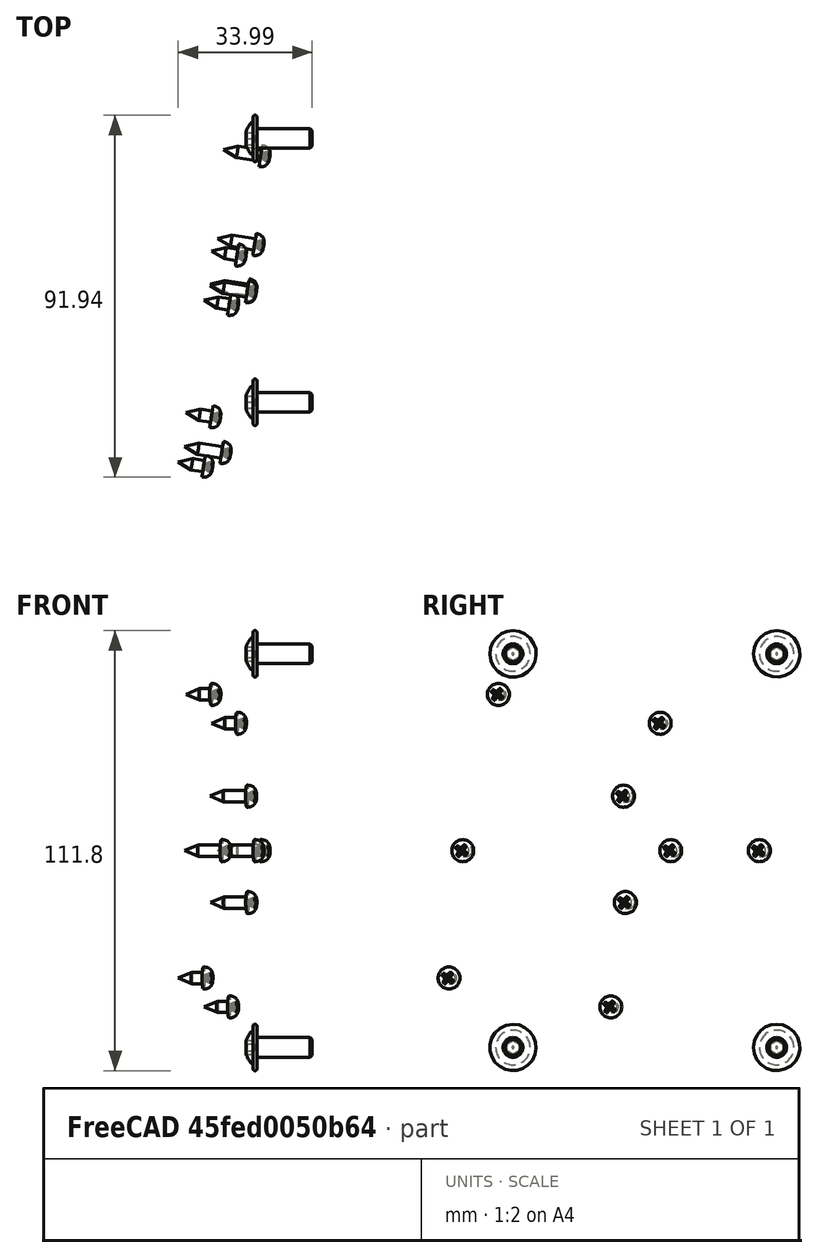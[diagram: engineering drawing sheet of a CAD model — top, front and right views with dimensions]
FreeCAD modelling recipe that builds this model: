
FCSTD DOCUMENT  (FreeCAD 1.0R39319 (Git))
Label: Assy_Stack_Module_Cover_forInserts
License: All rights reserved
LicenseURL: https://en.wikipedia.org/wiki/All_rights_reserved
objects: Part::FeaturePython×13, TechDraw::DrawViewBalloon×13, App::Link×8, TechDraw::DrawProjGroupItem×7, App::DocumentObjectGroup×3, TechDraw::DrawViewDimension×3, TechDraw::DrawSVGTemplate×2, TechDraw::DrawPage×2, PartDesign::CoordinateSystem×1, App::FeaturePython×1, App::Part×1, Spreadsheet::Sheet×1, TechDraw::DrawViewSpreadsheet×1, TechDraw::DrawProjGroup×1
note: 20 computed .brp shape members not serialized (recipe doc carries the construction recipe); baked Part::Feature solids carry a one-line shape summary decoded from their .brp
EXTERNAL_REF file=../../Part/Print/Stack_Module_Cover_forInserts.FCStd obj=stack_att
EXTERNAL_REF file=../../Part/Print/Stack_Module_Cover_forInserts.FCStd obj=Part
EXTERNAL_REF file=../../Part/Purchase/M5x12_Sleeve_Nut.FCStd obj=LCS_1
EXTERNAL_REF file=../../Part/Print/Stack_Module_Cover_forInserts.FCStd obj=sleevenut_att1
EXTERNAL_REF file=../../Part/Purchase/M5x12_Sleeve_Nut.FCStd obj=Part
EXTERNAL_REF file=../../Part/Print/Stack_Module_Cover_forInserts.FCStd obj=sleevenut_att2
EXTERNAL_REF file=../../Part/Print/Stack_Module_Cover_forInserts.FCStd obj=sleevenut_att3
EXTERNAL_REF file=../../Part/Print/Stack_Module_Cover_forInserts.FCStd obj=sleevenut_att4
EXTERNAL_REF file=../../Part/Print/Stack_Module_Cover_LogoTee.FCStd obj=LCS_1
EXTERNAL_REF file=../../Part/Print/Stack_Module_Cover_forInserts.FCStd obj=tee_att
EXTERNAL_REF file=../../Part/Print/Stack_Module_Cover_LogoTee.FCStd obj=Part
EXTERNAL_REF file=../../Part/Print/Stack_Module_Cover_LogoBall.FCStd obj=LCS_1
EXTERNAL_REF file=../../Part/Print/Stack_Module_Cover_forInserts.FCStd obj=Logo_att
EXTERNAL_REF file=../../Part/Print/Stack_Module_Cover_LogoBall.FCStd obj=Part
EXTERNAL_REF file=../../Part/Print/Stack_Module_Cover_insert.FCStd obj=LCS_1
EXTERNAL_REF file=../../Part/Print/Stack_Module_Cover_insert.FCStd obj=Part

FEATURE [App::DocumentObjectGroup] Parts
FEATURE [PartDesign::CoordinateSystem] LCS_Origin
  AttacherType = Attacher::AttachEngine3D
  AttachmentSupport = -> [X_Axis]
  MapMode = 2
FEATURE [App::DocumentObjectGroup] Constraints
FEATURE [App::FeaturePython] Variables  # WARN: FeaturePython — macro-defined, semantics opaque (R4)
  Type = App::PropertyContainer
FEATURE [App::DocumentObjectGroup] Configurations
FEATURE [App::Link] Stack_Module_Cover_twoInserts
  AttachedBy = #stack_att
  AttachedTo = Parent Assembly#LCS_Origin
  AttachmentOffset = pos=(0,0,0) rot=(0.57735,0.57735,-0.57735;4.18879rad)
  LinkPlacement = pos=(-4e-16,62.5,-63.5) rot=(0.57735,0.57735,-0.57735;2.0944rad)
  LinkedObject = -> <external ../../Part/Print/Stack_Module_Cover_forInserts.FCStd>#Part
  Placement = pos=(-4e-16,62.5,-63.5) rot=(0.57735,0.57735,-0.57735;2.0944rad)
  SolverId = Asm4EE
  expr: Placement = LCS_Origin.Placement * AttachmentOffset * Stack_Module_Cover_forInserts#stack_att.Placement ^ -1
FEATURE [App::Link] M5x12_Sleeve_Nut
  AttachedBy = #LCS_1
  AttachedTo = Stack_Module_Cover_twoInserts#sleevenut_att1
  AttachmentOffset = pos=(0,0,0) rot=(0,1,0;3.14159rad)
  LinkPlacement = pos=(-8,116,-130) rot=(-0.707107,0,0.707107;3.14159rad)
  LinkedObject = -> <external ../../Part/Purchase/M5x12_Sleeve_Nut.FCStd>#Part
  Placement = pos=(-8,116,-130) rot=(-0.707107,0,0.707107;3.14159rad)
  SolverId = Asm4EE
  expr: Placement = Stack_Module_Cover_twoInserts.Placement * Stack_Module_Cover_forInserts#sleevenut_att1.Placement * AttachmentOffset * M5x12_Sleeve_Nut#LCS_1.Placement ^ -1
FEATURE [App::Link] M5x12_Sleeve_Nut001
  AttachedBy = #LCS_1
  AttachedTo = Stack_Module_Cover_twoInserts#sleevenut_att2
  AttachmentOffset = pos=(0,0,0) rot=(0,1,0;3.14159rad)
  LinkPlacement = pos=(-8,2.84e-14,-127) rot=(-0.707107,0,0.707107;3.14159rad)
  LinkedObject = -> <external ../../Part/Purchase/M5x12_Sleeve_Nut.FCStd>#Part
  Placement = pos=(-8,2.84e-14,-127) rot=(-0.707107,0,0.707107;3.14159rad)
  SolverId = Asm4EE
  expr: Placement = Stack_Module_Cover_twoInserts.Placement * Stack_Module_Cover_forInserts#sleevenut_att2.Placement * AttachmentOffset * M5x12_Sleeve_Nut#LCS_1.Placement ^ -1
FEATURE [App::Link] M5x12_Sleeve_Nut002
  AttachedBy = #LCS_1
  AttachedTo = Stack_Module_Cover_twoInserts#sleevenut_att3
  LinkPlacement = pos=(-8,1.42e-14,-1.47e-14) rot=(0,-1,0;1.5708rad)
  LinkedObject = -> <external ../../Part/Purchase/M5x12_Sleeve_Nut.FCStd>#Part
  Placement = pos=(-8,1.42e-14,-1.47e-14) rot=(0,-1,0;1.5708rad)
  SolverId = Asm4EE
  expr: Placement = Stack_Module_Cover_twoInserts.Placement * Stack_Module_Cover_forInserts#sleevenut_att3.Placement * AttachmentOffset * M5x12_Sleeve_Nut#LCS_1.Placement ^ -1
FEATURE [App::Link] M5x12_Sleeve_Nut003
  AttachedBy = #LCS_1
  AttachedTo = Stack_Module_Cover_twoInserts#sleevenut_att4
  LinkPlacement = pos=(-8,116,3) rot=(0,-1,0;1.5708rad)
  LinkedObject = -> <external ../../Part/Purchase/M5x12_Sleeve_Nut.FCStd>#Part
  Placement = pos=(-8,116,3) rot=(0,-1,0;1.5708rad)
  SolverId = Asm4EE
  expr: Placement = Stack_Module_Cover_twoInserts.Placement * Stack_Module_Cover_forInserts#sleevenut_att4.Placement * AttachmentOffset * M5x12_Sleeve_Nut#LCS_1.Placement ^ -1
FEATURE [App::Link] Stack_Module_Cover_LogoTee
  AttachedBy = #LCS_1
  AttachedTo = Stack_Module_Cover_twoInserts#tee_att
  LinkPlacement = pos=(-22.5417,59.55,-63.5) rot=(-0.706014,0.055565,0.706014;3.03058rad)
  LinkedObject = -> <external ../../Part/Print/Stack_Module_Cover_LogoTee.FCStd>#Part
  Placement = pos=(-22.5417,59.55,-63.5) rot=(-0.706014,0.055565,0.706014;3.03058rad)
  SolverId = Asm4EE
  expr: Placement = Stack_Module_Cover_twoInserts.Placement * Stack_Module_Cover_forInserts#tee_att.Placement * AttachmentOffset * Stack_Module_Cover_LogoTee#LCS_1.Placement ^ -1
FEATURE [App::Link] Stack_Module_Cover_LogoBall
  AttachedBy = #LCS_1
  AttachedTo = Stack_Module_Cover_twoInserts#Logo_att
  AttachmentOffset = pos=(0,0,0) rot=(0,1,0;3.14159rad)
  LinkPlacement = pos=(-22.7075,58.503,-63.5) rot=(-0.706014,0.055565,0.706014;3.03058rad)
  LinkedObject = -> <external ../../Part/Print/Stack_Module_Cover_LogoBall.FCStd>#Part
  Placement = pos=(-22.7075,58.503,-63.5) rot=(-0.706014,0.055565,0.706014;3.03058rad)
  SolverId = Asm4EE
  expr: Placement = Stack_Module_Cover_twoInserts.Placement * Stack_Module_Cover_forInserts#Logo_att.Placement * AttachmentOffset * Stack_Module_Cover_LogoBall#LCS_1.Placement ^ -1
FEATURE [App::Link] Stack_Module_Cover_insert
  AttachedBy = #LCS_1
  AttachedTo = Stack_Module_Cover_twoInserts#Logo_att
  LinkPlacement = pos=(-22.7075,58.503,-63.5) rot=(0.553126,-0.543555,0.631347;3.98786rad)
  LinkedObject = -> <external ../../Part/Print/Stack_Module_Cover_insert.FCStd>#Part
  Placement = pos=(-22.7075,58.503,-63.5) rot=(0.553126,-0.543555,0.631347;3.98786rad)
  SolverId = Asm4EE
  expr: Placement = Stack_Module_Cover_twoInserts.Placement * Stack_Module_Cover_forInserts#Logo_att.Placement * AttachmentOffset * Stack_Module_Cover_insert#LCS_1.Placement ^ -1
FEATURE [Part::FeaturePython] Screw  label="M5x14-Screw"  # WARN: FeaturePython — macro-defined, semantics opaque (R4)
  BaseObject = -> Stack_Module_Cover_twoInserts [Body.Pocket022.Edge443]
  Diameter = 3
  Invert = false
  LeftHanded = false
  Length = 3
  LengthCustom = 14
  MatchOuter = false
  OffsetAngle = 0
  Placement = pos=(-4.5,113.5,-13.5) rot=(0,-1,0;1.5708rad)
  Thread = false
  Type = 86
FEATURE [Part::FeaturePython] Screw001  label="M5x14-Screw007"  # WARN: FeaturePython — macro-defined, semantics opaque (R4)
  BaseObject = -> Stack_Module_Cover_twoInserts [Body.Pocket022.Edge441]
  Diameter = 3
  Invert = false
  LeftHanded = false
  Length = 3
  LengthCustom = 14
  MatchOuter = false
  OffsetAngle = 0
  Placement = pos=(-4.5,46.5,-13.5) rot=(0,-1,0;1.5708rad)
  Thread = false
  Type = 86
FEATURE [Part::FeaturePython] Screw002  label="M5x14-Screw008"  # WARN: FeaturePython — macro-defined, semantics opaque (R4)
  BaseObject = -> Stack_Module_Cover_twoInserts [Body.Pocket022.Edge440]
  Diameter = 3
  Invert = true
  LeftHanded = false
  Length = 3
  LengthCustom = 14
  MatchOuter = false
  OffsetAngle = 0
  Placement = pos=(-4.5,46.5,-113.5) rot=(0,-1,0;1.5708rad)
  Thread = false
  Type = 86
FEATURE [Part::FeaturePython] Screw003  label="M5x14-Screw009"  # WARN: FeaturePython — macro-defined, semantics opaque (R4)
  BaseObject = -> Stack_Module_Cover_twoInserts [Body.Pocket022.Edge442]
  Diameter = 3
  Invert = true
  LeftHanded = false
  Length = 3
  LengthCustom = 14
  MatchOuter = false
  OffsetAngle = 0
  Placement = pos=(-4.5,113.5,-113.5) rot=(0,-1,0;1.5708rad)
  Thread = false
  Type = 86
FEATURE [Part::FeaturePython] Screw004  label="ST2.9x9.5-Screw"  # WARN: FeaturePython — macro-defined, semantics opaque (R4)
  BaseObject = -> Stack_Module_Cover_twoInserts [Body.Pocket022.Edge623]
  Diameter = 2
  Invert = true
  LeftHanded = false
  Length = 1
  LengthCustom = 9.5
  MatchOuter = false
  OffsetAngle = 0
  Placement = pos=(-3.55191,109.13,-63.5) rot=(0.156434,0.987688,0;1.5708rad)
  Thread = false
  Type = 81
FEATURE [Part::FeaturePython] Screw005  label="ST2.9x9.5-Screw009"  # WARN: FeaturePython — macro-defined, semantics opaque (R4)
  BaseObject = -> Stack_Module_Cover_insert [Body.Pocket001.Edge17]
  Diameter = 2
  Invert = true
  LeftHanded = false
  Length = 1
  LengthCustom = 9.5
  MatchOuter = false
  OffsetAngle = 0
  Placement = pos=(-5.0963,86.5939,-63.5) rot=(0.156434,0.987688,0;1.5708rad)
  Thread = false
  Type = 81
FEATURE [Part::FeaturePython] Screw006  label="ST2.9x9.5-Screw010"  # WARN: FeaturePython — macro-defined, semantics opaque (R4)
  BaseObject = -> Stack_Module_Cover_insert [Body.Pocket001.Edge16]
  Diameter = 2
  Invert = true
  LeftHanded = false
  Length = 1
  LengthCustom = 9.5
  MatchOuter = false
  OffsetAngle = 0
  Placement = pos=(-6.92025,75.0779,-76.6923) rot=(0.156434,0.987688,0;1.5708rad)
  Thread = false
  Type = 81
FEATURE [Part::FeaturePython] Screw007  label="ST2.9x9.5-Screw011"  # WARN: FeaturePython — macro-defined, semantics opaque (R4)
  BaseObject = -> Stack_Module_Cover_insert [Body.Pocket001.Edge18]
  Diameter = 2
  Invert = true
  LeftHanded = false
  Length = 1
  LengthCustom = 9.5
  MatchOuter = false
  OffsetAngle = 0
  Placement = pos=(-6.99407,74.6118,-49.6583) rot=(0.156434,0.987688,0;1.5708rad)
  Thread = false
  Type = 81
FEATURE [Part::FeaturePython] Screw008  label="ST2.9x9.5-Screw012"  # WARN: FeaturePython — macro-defined, semantics opaque (R4)
  BaseObject = -> Stack_Module_Cover_insert [Body.Pocket001.Edge9]
  Diameter = 2
  Invert = true
  LeftHanded = false
  Length = 1
  LengthCustom = 9.5
  MatchOuter = false
  OffsetAngle = 0
  Placement = pos=(-13.4655,33.7525,-63.5) rot=(0.156434,0.987688,0;1.5708rad)
  Thread = false
  Type = 81
FEATURE [Part::FeaturePython] Screw009  label="ST2.9x6.5-Screw"  # WARN: FeaturePython — macro-defined, semantics opaque (R4)
  BaseObject = -> Stack_Module_Cover_twoInserts [Body.Pocket022.Edge118]
  Diameter = 2
  Invert = false
  LeftHanded = false
  Length = 0
  LengthCustom = 6.5
  MatchOuter = false
  Offset = 2
  OffsetAngle = 0
  Placement = pos=(-11.5578,71.3676,-103.202) rot=(0.156434,0.987688,0;1.5708rad)
  Thread = false
  Type = 81
FEATURE [Part::FeaturePython] Screw010  label="ST2.9x6.5-Screw012"  # WARN: FeaturePython — macro-defined, semantics opaque (R4)
  BaseObject = -> Stack_Module_Cover_twoInserts [Body.Pocket022.Edge121]
  Diameter = 2
  Invert = false
  LeftHanded = false
  Length = 0
  LengthCustom = 6.5
  MatchOuter = false
  Offset = 2
  OffsetAngle = 0
  Placement = pos=(-18.0667,30.2717,-95.8654) rot=(0.156434,0.987688,0;1.5708rad)
  Thread = false
  Type = 81
FEATURE [Part::FeaturePython] Screw011  label="ST2.9x6.5-Screw013"  # WARN: FeaturePython — macro-defined, semantics opaque (R4)
  BaseObject = -> Stack_Module_Cover_twoInserts [Body.Pocket022.Edge169]
  Diameter = 2
  Invert = false
  LeftHanded = false
  Length = 0
  LengthCustom = 6.5
  MatchOuter = false
  Offset = 2
  OffsetAngle = 0
  Placement = pos=(-16.0788,42.8227,-23.798) rot=(0.156434,0.987688,0;1.5708rad)
  Thread = false
  Type = 81
FEATURE [Part::FeaturePython] Screw012  label="ST2.9x6.5-Screw014"  # WARN: FeaturePython — macro-defined, semantics opaque (R4)
  BaseObject = -> Stack_Module_Cover_twoInserts [Body.Pocket022.Edge168]
  Diameter = 2
  Invert = false
  LeftHanded = false
  Length = 0
  LengthCustom = 6.5
  MatchOuter = false
  Offset = 2
  OffsetAngle = 0
  Placement = pos=(-9.5699,83.9185,-31.1346) rot=(0.156434,0.987688,0;1.5708rad)
  Thread = false
  Type = 81
FEATURE [App::Part] Assembly  label="Assy_Stack_Module_Cover_forInserts"
  AssemblyType = Part::Link
  Group = -> [LCS_Origin,Constraints,Variables,Configurations,Stack_Module_Cover_twoInserts,M5x12_Sleeve_Nut,M5x12_Sleeve_Nut001,M5x12_Sleeve_Nut002,M5x12_Sleeve_Nut003,Stack_Module_Cover_LogoTee,Stack_Module_Cover_LogoBall,Stack_Module_Cover_insert,Screw,Screw001,Screw002,Screw003,Screw004,Screw005,Screw006,Screw007,Screw008,Screw009,Screw010,Screw011,Screw012]
  Origin = -> Origin
  Type = Assembly
FEATURE [Spreadsheet::Sheet] Spreadsheet  label="BOM"
  cells = A1=6; B1=5; C1='M3x10 mm self-tapping screw; D1==10 mm; A2=5; B2=4; C2='M3x5 mm self-tapping screw; D2==5 mm; A3=4; B3=1; C3='Stack_Module_Cover_LogoBall; D3='-; E3='PETG or PLA; A4=3; B4=1; C4='Stack_Module_Cover_LogoTee; D4='-; E4='PETG or PLA; A5=2; B5=1; C5='Stack_Module_Cover_insert; D5='-; E5='PETG or PLA, white; A6=1; B6=1; C6='Stack_Module_Cover_forInserts; D6='-; E6='PETG or PLA; A7='Position; B7='Quantity; C7='Part; D7='Dimensions; E7='Material
FEATURE [TechDraw::DrawSVGTemplate] Template
  EditableTexts = approval_person=GitHubPR; creator=Stefan; date_of_issue=20.03.2026; document_type=Assembly Drawing; general_tolerances=na; identification_number=na; language_code=EN; part_material=na; revision_index=AAA; scale=1 : 1; sheet_number=1 / 1; title=Assy_Stack_Module_Cover_forInserts
  Height = 420
  Orientation = 1
  Template = <userpath>/Documents/PiTrac/3D Printed Parts/Enclosure Version 3/Assets/PiTrac_A2_Landscape_ISO5457_minimal.svg
  Width = 594
FEATURE [TechDraw::DrawViewSpreadsheet] Sheet
  CellEnd = E7
  CellStart = A1
  Font = osifont
  LineWidth = 0.35
  LockPosition = false
  Rotation = 0
  ScaleType = 2
  Source = -> Spreadsheet
  Symbol = <blob: 7887 chars omitted>
  TextSize = 12
  X = 496.686
  Y = 106.021
FEATURE [TechDraw::DrawProjGroupItem] View
  CoarseView = false
  Direction = (-0.57735,0.57735,-0.57735)
  Focus = 100
  HardHidden = false
  IsoCount = 0
  IsoHidden = false
  IsoVisible = false
  LockPosition = false
  Perspective = false
  Rotation = 0
  RotationVector = (1,0,0)
  Scale = 0.5
  ScaleType = 2
  ScrubCount = 1
  SeamHidden = false
  SeamVisible = false
  SmoothHidden = false
  SmoothVisible = true
  Source = -> [Assembly]
  Type = 0
  X = 339.537
  XDirection = (0,-0.707106,-0.707106)
  Y = 97.1596
FEATURE [TechDraw::DrawProjGroupItem] View001  label="Front"
  CoarseView = false
  Direction = (0,1,0)
  Focus = 100
  HardHidden = false
  IsoCount = 0
  IsoHidden = false
  IsoVisible = false
  LockPosition = true
  Perspective = false
  Rotation = 0
  RotationVector = (1,0,0)
  ScaleType = 2
  ScrubCount = 1
  SeamHidden = false
  SeamVisible = false
  SmoothHidden = false
  SmoothVisible = true
  Source = -> [Assembly]
  Type = 0
  X = 0
  XDirection = (0,0,-1)
  Y = 0
FEATURE [TechDraw::DrawProjGroupItem] ProjItem  label="Left"
  CoarseView = false
  Direction = (0,1e-16,1)
  Focus = 100
  HardHidden = false
  IsoCount = 0
  IsoHidden = false
  IsoVisible = false
  LockPosition = false
  Perspective = false
  Rotation = 0
  RotationVector = (1,0,0)
  ScaleType = 0
  ScrubCount = 1
  SeamHidden = false
  SeamVisible = false
  SmoothHidden = false
  SmoothVisible = true
  Source = -> [Assembly]
  Type = 1
  X = 159
  XDirection = (0,1,-1e-16)
  Y = 0
FEATURE [TechDraw::DrawProjGroupItem] ProjItem001  label="Top"
  CoarseView = false
  Direction = (-1,0,0)
  Focus = 100
  HardHidden = false
  IsoCount = 0
  IsoHidden = false
  IsoVisible = false
  LockPosition = false
  Perspective = false
  Rotation = 0
  RotationVector = (1,0,0)
  ScaleType = 0
  ScrubCount = 1
  SeamHidden = false
  SeamVisible = false
  SmoothHidden = false
  SmoothVisible = true
  Source = -> [Assembly]
  Type = 4
  X = 0
  XDirection = (0,0,-1)
  Y = -105.76
FEATURE [TechDraw::DrawProjGroupItem] ProjItem002  label="Rear"
  CoarseView = false
  Direction = (0,-1,0)
  Focus = 100
  HardHidden = false
  IsoCount = 0
  IsoHidden = false
  IsoVisible = false
  LockPosition = false
  Perspective = false
  Rotation = 0
  RotationVector = (1,0,0)
  ScaleType = 0
  ScrubCount = 1
  SeamHidden = false
  SeamVisible = false
  SmoothHidden = false
  SmoothVisible = true
  Source = -> [Assembly]
  Type = 3
  X = 318
  XDirection = (0,0,1)
  Y = 0
FEATURE [TechDraw::DrawProjGroupItem] ProjItem003  label="Bottom"
  CoarseView = false
  Direction = (1,0,0)
  Focus = 100
  HardHidden = false
  IsoCount = 0
  IsoHidden = false
  IsoVisible = false
  LockPosition = false
  Perspective = false
  Rotation = 0
  RotationVector = (1,0,0)
  ScaleType = 0
  ScrubCount = 1
  SeamHidden = false
  SeamVisible = false
  SmoothHidden = false
  SmoothVisible = true
  Source = -> [Assembly]
  Type = 5
  X = 0
  XDirection = (0,0,-1)
  Y = 105.76
FEATURE [TechDraw::DrawProjGroup] ProjGroup
  Anchor = -> View001
  AutoDistribute = true
  LockPosition = false
  ProjectionType = 0
  Rotation = 0
  ScaleType = 0
  Source = -> [Assembly]
  Views = -> [View001,ProjItem,ProjItem001,ProjItem002,ProjItem003]
  X = 165.254
  Y = 222.997
  spacingX = 15
  spacingY = 15
FEATURE [TechDraw::DrawViewBalloon] Balloon
  BubbleShape = 0
  EndType = 0
  EndTypeScale = 1
  KinkLength = 5
  LockPosition = false
  OriginX = -41.8317
  OriginY = -30.0185
  Rotation = 0
  ScaleType = 0
  ShapeScale = 1
  SourceView = -> ProjItem001
  Text = 1
  TextWrapLen = -1
  X = -90
  Y = -22.3266
FEATURE [TechDraw::DrawViewBalloon] Balloon001
  BubbleShape = 0
  EndType = 0
  EndTypeScale = 1
  KinkLength = 5
  LockPosition = false
  OriginX = -24.0534
  OriginY = 6.56381
  Rotation = 0
  ScaleType = 0
  ShapeScale = 1
  SourceView = -> ProjItem001
  Text = 2
  TextWrapLen = -1
  X = -90
  Y = -3.86449
FEATURE [TechDraw::DrawViewBalloon] Balloon002
  BubbleShape = 0
  EndType = 0
  EndTypeScale = 1
  KinkLength = 5
  LockPosition = false
  OriginX = -3.88181
  OriginY = -45.4036
  Rotation = 0
  ScaleType = 0
  ShapeScale = 1
  SourceView = -> Balloon001
  Text = 3
  TextWrapLen = -1
  X = -90
  Y = -46.6009
FEATURE [TechDraw::DrawViewBalloon] Balloon003
  BubbleShape = 0
  EndType = 0
  EndTypeScale = 1
  KinkLength = 5
  LockPosition = false
  OriginX = -29.8655
  OriginY = 27.4192
  Rotation = 0
  ScaleType = 0
  ShapeScale = 1
  SourceView = -> Balloon002
  Text = 4
  TextWrapLen = -1
  X = -90
  Y = 18.0165
FEATURE [TechDraw::DrawViewBalloon] Balloon004
  BubbleShape = 0
  EndType = 0
  EndTypeScale = 1
  KinkLength = 5
  LockPosition = false
  OriginX = -39.2761
  OriginY = -19.3115
  Rotation = 0
  ScaleType = 0
  ShapeScale = 1
  SourceView = -> ProjItem003
  Text = 5
  TextWrapLen = -1
  X = -90
  Y = -14.9656
FEATURE [TechDraw::DrawViewBalloon] Balloon005
  BubbleShape = 0
  EndType = 0
  EndTypeScale = 1
  KinkLength = 5
  LockPosition = false
  OriginX = -31.8217
  OriginY = 21.8737
  Rotation = 0
  ScaleType = 0
  ShapeScale = 1
  SourceView = -> Balloon004
  Text = 5
  TextWrapLen = -1
  X = -90
  Y = 21.0016
FEATURE [TechDraw::DrawViewBalloon] Balloon006
  BubbleShape = 0
  EndType = 0
  EndTypeScale = 1
  KinkLength = 5
  LockPosition = false
  OriginX = 33.031
  OriginY = -33.2883
  Rotation = 0
  ScaleType = 0
  ShapeScale = 1
  SourceView = -> Balloon005
  Text = 5
  TextWrapLen = -1
  X = 90
  Y = -64.3506
FEATURE [TechDraw::DrawViewBalloon] Balloon007
  BubbleShape = 0
  EndType = 0
  EndTypeScale = 1
  KinkLength = 5
  LockPosition = false
  OriginX = 40.6717
  OriginY = 7.89686
  Rotation = 0
  ScaleType = 0
  ShapeScale = 1
  SourceView = -> Balloon006
  Text = 5
  TextWrapLen = -1
  X = 90
  Y = -30.0606
FEATURE [TechDraw::DrawViewBalloon] Balloon008
  BubbleShape = 0
  EndType = 0
  EndTypeScale = 1
  KinkLength = 5
  LockPosition = false
  OriginX = 0.231897
  OriginY = 46.473
  Rotation = 0
  ScaleType = 0
  ShapeScale = 1
  SourceView = -> Balloon007
  Text = 6
  TextWrapLen = -1
  X = 90
  Y = 47.0918
FEATURE [TechDraw::DrawViewBalloon] Balloon009
  BubbleShape = 0
  EndType = 0
  EndTypeScale = 1
  KinkLength = 5
  LockPosition = false
  OriginX = -0.14082
  OriginY = 24.11
  Rotation = 0
  ScaleType = 0
  ShapeScale = 1
  SourceView = -> ProjItem003
  Text = 6
  TextWrapLen = -1
  X = 90
  Y = 32.5558
FEATURE [TechDraw::DrawViewBalloon] Balloon010
  BubbleShape = 0
  EndType = 0
  EndTypeScale = 1
  KinkLength = 5
  LockPosition = false
  OriginX = 13.8361
  OriginY = 12.5558
  Rotation = 0
  ScaleType = 0
  ShapeScale = 1
  SourceView = -> Balloon009
  Text = 6
  TextWrapLen = -1
  X = 90
  Y = 16.529
FEATURE [TechDraw::DrawViewBalloon] Balloon011
  BubbleShape = 0
  EndType = 0
  EndTypeScale = 1
  KinkLength = 5
  LockPosition = false
  OriginX = -13.1859
  OriginY = 12.9285
  Rotation = 0
  ScaleType = 0
  ShapeScale = 1
  SourceView = -> Balloon010
  Text = 6
  TextWrapLen = -1
  X = -90
  Y = 5.72021
FEATURE [TechDraw::DrawViewBalloon] Balloon012
  BubbleShape = 0
  EndType = 0
  EndTypeScale = 1
  KinkLength = 5
  LockPosition = false
  OriginX = -0.886254
  OriginY = -27.6976
  Rotation = 0
  ScaleType = 0
  ShapeScale = 1
  SourceView = -> Balloon011
  Text = 6
  TextWrapLen = -1
  X = -90
  Y = -39.5649
FEATURE [TechDraw::DrawViewDimension] Dimension
  AngleOverride = false
  Arbitrary = false
  ArbitraryTolerances = false
  BoxCorners = (2) [(-70,-16.0101,-1e-07),(70,16.0101,1e-07)]
  EqualTolerance = true
  ExtensionAngle = 0
  FormatSpec = %.2w
  FormatSpecOverTolerance = %+.2w
  FormatSpecUnderTolerance = %+.2w
  Inverted = false
  LineAngle = 0
  LockPosition = false
  MeasureType = 1
  OverTolerance = 0
  References2D = -> [ProjItem]
  Rotation = 0
  ScaleType = 0
  TheoreticalExact = false
  Type = 0
  UnderTolerance = 0
  X = 0
  Y = -52.3681
FEATURE [TechDraw::DrawViewDimension] Dimension001
  AngleOverride = false
  Arbitrary = false
  ArbitraryTolerances = false
  BoxCorners = (2) [(-74,-16.0101,-1e-07),(74,16.0101,1e-07)]
  EqualTolerance = true
  ExtensionAngle = 0
  FormatSpec = %.2w
  FormatSpecOverTolerance = %+.2w
  FormatSpecUnderTolerance = %+.2w
  Inverted = false
  LineAngle = 0
  LockPosition = false
  MeasureType = 1
  OverTolerance = 0
  References2D = -> [ProjItem002]
  Rotation = 0
  ScaleType = 0
  TheoreticalExact = false
  Type = 0
  UnderTolerance = 0
  X = 88.8831
  Y = -0.010122
FEATURE [TechDraw::DrawViewDimension] Dimension002
  AngleOverride = false
  Arbitrary = false
  ArbitraryTolerances = false
  BoxCorners = (2) [(-74,-70,-1e-07),(74,70,1e-07)]
  EqualTolerance = true
  ExtensionAngle = 0
  FormatSpec = %.2w
  FormatSpecOverTolerance = %+.2w
  FormatSpecUnderTolerance = %+.2w
  Inverted = false
  LineAngle = 0
  LockPosition = false
  MeasureType = 1
  OverTolerance = 0
  References2D = -> [ProjItem001]
  Rotation = 0
  ScaleType = 0
  TheoreticalExact = false
  Type = 0
  UnderTolerance = 0
  X = 0
  Y = -89.7283
FEATURE [TechDraw::DrawPage] Page
  KeepUpdated = true
  NextBalloonIndex = 14
  ProjectionType = 0
  Template = -> Template
  Views = -> [Sheet,View,ProjGroup,Balloon,Balloon001,Balloon002,Balloon003,Balloon004,Balloon005,Balloon006,Balloon007,Balloon008,Balloon009,Balloon010,Balloon011,Balloon012,Dimension,Dimension001,Dimension002]
FEATURE [TechDraw::DrawSVGTemplate] Template001
  Height = 210
  Orientation = 1
  Template = C:/Program Files/FreeCAD 1.0/data/Mod/TechDraw/Templates/Default_Template_A4_Landscape.svg
  Width = 297
FEATURE [TechDraw::DrawProjGroupItem] View002
  CoarseView = false
  Direction = (-0.57735,0.57735,-0.57735)
  Focus = 100
  HardHidden = false
  IsoCount = 0
  IsoHidden = false
  IsoVisible = false
  LockPosition = false
  Perspective = false
  Rotation = 0
  RotationVector = (1,0,0)
  ScaleType = 0
  ScrubCount = 1
  SeamHidden = false
  SeamVisible = false
  SmoothHidden = false
  SmoothVisible = true
  Source = -> [Assembly]
  Type = 0
  X = 148.5
  XDirection = (0,-0.707106,-0.707106)
  Y = 105
FEATURE [TechDraw::DrawPage] Page001
  KeepUpdated = true
  NextBalloonIndex = 1
  ProjectionType = 0
  Template = -> Template001
  Views = -> [View002]

RESOLVED EXTERNAL PARTS (link-assembly join: the EXTERNAL_REF files above that resolve inside this repo's crawl, each included once):
---- part ../../Part/Print/Stack_Module_Cover_LogoBall.FCStd = doc fcstd_3ce8b7379f39 ----
FCSTD DOCUMENT  (FreeCAD 1.0R39319 (Git))
Label: Stack_Module_Cover_LogoBall
License: All rights reserved
LicenseURL: https://en.wikipedia.org/wiki/All_rights_reserved
objects: Sketcher::SketchObject×2, PartDesign::Pad×2, PartDesign::ShapeBinder×1, PartDesign::Body×1, Part::Scale×1, PartDesign::CoordinateSystem×1, App::Part×1
note: 14 computed .brp shape members not serialized (recipe doc carries the construction recipe); baked Part::Feature solids carry a one-line shape summary decoded from their .brp

FEATURE [Sketcher::SketchObject] Sketch
  ArcFitTolerance = 1e-06
  AttachmentSupport = -> [XY_Plane001]
  FullyConstrained = false
  MakeInternals = false
  MapMode = 5
  sketch-geometry (161):
    g0: Circle CenterX=0 CenterY=0 CenterZ=0 NormalX=0 NormalY=0 NormalZ=1 AngleXU=0 Radius=41
    g1: Circle [constr] CenterX=0 CenterY=0 CenterZ=0 NormalX=0 NormalY=0 NormalZ=1 AngleXU=0 Radius=37.5
    g2: LineSegment StartX=24.9449 StartY=28 StartZ=0 EndX=-10.8953 EndY=28 EndZ=0
    g3: LineSegment StartX=-23.8473 StartY=19.3147 StartZ=0 EndX=-26.5337 EndY=12.7677 EndZ=0
    g4: ArcOfCircle CenterX=-10.8953 CenterY=14 CenterZ=0 NormalX=0 NormalY=0 NormalZ=1 AngleXU=0 Radius=14 StartAngle=1.5708 EndAngle=2.75221
    g5: GeomPoint [constr] X=-20.2834 Y=28 Z=0
    g6: ArcOfCircle CenterX=-25.5341 CenterY=12.1792 CenterZ=0 NormalX=0 NormalY=0 NormalZ=1 AngleXU=0 Radius=1.16 StartAngle=2.60947 EndAngle=5.75448
    g7: LineSegment StartX=-24.5325 StartY=11.594 StartZ=0 EndX=-20.8221 EndY=16.5323 EndZ=0
    g8: LineSegment StartX=-15.8813 StartY=19 StartZ=0 EndX=-10.5 EndY=19 EndZ=0
    g9: ArcOfCircle CenterX=-15.8813 CenterY=12.82 CenterZ=0 NormalX=0 NormalY=0 NormalZ=1 AngleXU=0 Radius=6.18 StartAngle=1.5708 EndAngle=2.49722
    g10: GeomPoint [constr] X=-18.9679 Y=19 Z=0
    g11: LineSegment StartX=-10.5 StartY=19 StartZ=0 EndX=-13.1153 EndY=-2.30004 EndZ=0
    g12: LineSegment StartX=-19.3069 StartY=-16.5524 StartZ=0 EndX=-15.1543 EndY=-8.75786 EndZ=0
    g13: ArcOfCircle CenterX=-31.5171 CenterY=-0.0405907 CenterZ=0 NormalX=0 NormalY=0 NormalZ=1 AngleXU=0 Radius=18.54 StartAngle=5.79368 EndAngle=6.16101
    g14: GeomPoint [constr] X=-13.535 Y=-5.71833 Z=0
    g15: ArcOfCircle CenterX=-14.5498 CenterY=-19.0867 CenterZ=0 NormalX=0 NormalY=0 NormalZ=1 AngleXU=0 Radius=5.39 StartAngle=2.65209 EndAngle=5.73645
    g16: ArcOfCircle CenterX=-19.2458 CenterY=-16.2287 CenterZ=0 NormalX=0 NormalY=0 NormalZ=1 AngleXU=0 Radius=10.8873 StartAngle=5.73645 EndAngle=6.16101
    g17: LineSegment StartX=-8.43962 StartY=-17.5555 StartZ=0 EndX=-3.95119 EndY=19 EndZ=0
    g18: LineSegment StartX=-3.95119 StartY=19 StartZ=0 EndX=8.04881 EndY=19 EndZ=0
    g19: Ellipse CenterX=34.0387 CenterY=-11.7205 CenterZ=0 NormalX=0 NormalY=0 NormalZ=1 MajorRadius=2.25 MinorRadius=0.6 AngleXU=1.23918
    g20: LineSegment [constr] StartX=34.7712 StartY=-9.59304 StartZ=0 EndX=33.3061 EndY=-13.8479 EndZ=0
    g21: LineSegment [constr] StartX=33.4714 StartY=-11.5251 StartZ=0 EndX=34.606 EndY=-11.9158 EndZ=0
    g22: GeomPoint [constr] X=34.7447 Y=-9.67008 Z=0
    g23: GeomPoint [constr] X=33.3327 Y=-13.7708 Z=0
    g24: Ellipse CenterX=6.34131 CenterY=-29.8335 CenterZ=0 NormalX=0 NormalY=0 NormalZ=1 MajorRadius=2.1 MinorRadius=1.4 AngleXU=0.20944
    g25: LineSegment [constr] StartX=8.39542 StartY=-29.3969 StartZ=0 EndX=4.2872 EndY=-30.2701 EndZ=0
    g26: LineSegment [constr] StartX=6.05023 StartY=-28.4641 StartZ=0 EndX=6.63239 EndY=-31.2029 EndZ=0
    g27: GeomPoint [constr] X=7.87235 Y=-29.5081 Z=0
    g28: GeomPoint [constr] X=4.81027 Y=-30.1589 Z=0
    g29: Ellipse CenterX=13.4858 CenterY=-33.3786 CenterZ=0 NormalX=0 NormalY=0 NormalZ=1 MajorRadius=2.05 MinorRadius=1.15 AngleXU=0.383973
    g30: LineSegment [constr] StartX=15.3866 StartY=-32.6107 StartZ=0 EndX=11.5851 EndY=-34.1466 EndZ=0
    g31: LineSegment [constr] StartX=13.055 StartY=-32.3124 StartZ=0 EndX=13.9166 EndY=-34.4449 EndZ=0
    g32: GeomPoint [constr] X=15.0593 Y=-32.7429 Z=0
    g33: GeomPoint [constr] X=11.9124 Y=-34.0143 Z=0
    g34: Ellipse CenterX=21.6653 CenterY=-28.7509 CenterZ=0 NormalX=0 NormalY=0 NormalZ=1 MajorRadius=1.875 MinorRadius=1.15 AngleXU=0.645772
    g35: LineSegment [constr] StartX=23.1628 StartY=-27.6225 StartZ=0 EndX=20.1679 EndY=-29.8793 EndZ=0
    g36: LineSegment [constr] StartX=20.9732 StartY=-27.8325 StartZ=0 EndX=22.3574 EndY=-29.6693 EndZ=0
    g37: GeomPoint [constr] X=22.8481 Y=-27.8596 Z=0
    g38: GeomPoint [constr] X=20.4826 Y=-29.6421 Z=0
    g39: Ellipse CenterX=28.9341 CenterY=-18.79 CenterZ=0 NormalX=0 NormalY=0 NormalZ=1 MajorRadius=2 MinorRadius=1.1 AngleXU=0.994838
    g40: LineSegment [constr] StartX=30.0234 StartY=-17.1127 StartZ=0 EndX=27.8449 EndY=-20.4674 EndZ=0
    g41: LineSegment [constr] StartX=28.0116 StartY=-18.1909 StartZ=0 EndX=29.8567 EndY=-19.3891 EndZ=0
    g42: GeomPoint [constr] X=29.8439 Y=-17.3892 Z=0
    g43: GeomPoint [constr] X=28.0244 Y=-20.1909 Z=0
    g44: Ellipse CenterX=-1.5703 CenterY=-35.9657 CenterZ=0 NormalX=0 NormalY=0 NormalZ=1 MajorRadius=2.50238 MinorRadius=1.30124 AngleXU=-0.0436333
    g45: LineSegment [constr] StartX=0.929699 StartY=-36.0749 StartZ=0 EndX=-4.0703 EndY=-35.8566 EndZ=0
    g46: LineSegment [constr] StartX=-1.51354 StartY=-34.6657 StartZ=0 EndX=-1.62706 EndY=-37.2657 EndZ=0
    g47: GeomPoint [constr] X=0.565114 Y=-36.059 Z=0
    g48: GeomPoint [constr] X=-3.70572 Y=-35.8725 Z=0
    g49: Ellipse CenterX=-8.52046 CenterY=-28.7646 CenterZ=0 NormalX=0 NormalY=0 NormalZ=1 MajorRadius=2.25 MinorRadius=1.5 AngleXU=-0.287979
    g50: LineSegment [constr] StartX=-6.36312 StartY=-29.4036 StartZ=0 EndX=-10.6778 EndY=-28.1256 EndZ=0
    g51: LineSegment [constr] StartX=-8.09444 StartY=-27.3264 StartZ=0 EndX=-8.94648 EndY=-30.2028 EndZ=0
    g52: GeomPoint [constr] X=-6.91247 Y=-29.2409 Z=0
    g53: GeomPoint [constr] X=-10.1284 Y=-28.2883 Z=0
    g54: Ellipse CenterX=-17.4531 CenterY=-31.4863 CenterZ=0 NormalX=0 NormalY=0 NormalZ=1 MajorRadius=2.15 MinorRadius=1 AngleXU=-0.506145
    g55: LineSegment [constr] StartX=-15.5727 StartY=-32.5287 StartZ=0 EndX=-19.3336 EndY=-30.444 EndZ=0
    g56: LineSegment [constr] StartX=-16.9683 StartY=-30.6117 StartZ=0 EndX=-17.938 EndY=-32.3609 EndZ=0
    g57: GeomPoint [constr] X=-15.7885 Y=-32.409 Z=0
    g58: GeomPoint [constr] X=-19.1178 Y=-30.5636 Z=0
    g59: Ellipse CenterX=-26.3287 CenterY=-24.552 CenterZ=0 NormalX=0 NormalY=0 NormalZ=1 MajorRadius=2.15 MinorRadius=0.9 AngleXU=-0.820304
    g60: LineSegment [constr] StartX=-24.8624 StartY=-26.1244 StartZ=0 EndX=-27.795 EndY=-22.9795 EndZ=0
    g61: LineSegment [constr] StartX=-25.6705 StartY=-23.9382 StartZ=0 EndX=-26.9869 EndY=-25.1658 EndZ=0
    g62: GeomPoint [constr] X=-24.9971 Y=-25.98 Z=0
    g63: GeomPoint [constr] X=-27.6604 Y=-23.1239 Z=0
    g64: Ellipse CenterX=-35.9329 CenterY=-2.19776 CenterZ=0 NormalX=0 NormalY=0 NormalZ=1 MajorRadius=2.45458 MinorRadius=0.601121 AngleXU=-1.50971
    g65: LineSegment [constr] StartX=-35.783 StartY=-4.64776 StartZ=0 EndX=-36.0827 EndY=0.252235 EndZ=0
    g66: LineSegment [constr] StartX=-35.3329 StartY=-2.16107 StartZ=0 EndX=-36.5329 EndY=-2.23446 EndZ=0
    g67: GeomPoint [constr] X=-35.7876 Y=-4.57316 Z=0
    g68: GeomPoint [constr] X=-36.0781 Y=0.17763 Z=0
    g69: Ellipse CenterX=-25.5794 CenterY=-16.6115 CenterZ=0 NormalX=0 NormalY=0 NormalZ=1 MajorRadius=2.5 MinorRadius=1.55 AngleXU=-0.994837
    g70: LineSegment [constr] StartX=-24.2178 StartY=-18.7082 StartZ=0 EndX=-26.941 EndY=-14.5148 EndZ=0
    g71: LineSegment [constr] StartX=-24.2795 StartY=-15.7673 StartZ=0 EndX=-26.8794 EndY=-17.4557 EndZ=0
    g72: GeomPoint [constr] X=-24.5111 Y=-18.2566 Z=0
    g73: GeomPoint [constr] X=-26.6478 Y=-14.9664 Z=0
    g74: Ellipse CenterX=-31.3328 CenterY=-17.7272 CenterZ=0 NormalX=0 NormalY=0 NormalZ=1 MajorRadius=1.75 MinorRadius=0.6 AngleXU=-1.05592
    g75: LineSegment [constr] StartX=-30.4711 StartY=-19.2504 StartZ=0 EndX=-32.1945 EndY=-16.2041 EndZ=0
    g76: LineSegment [constr] StartX=-30.8106 StartY=-17.4318 StartZ=0 EndX=-31.855 EndY=-18.0227 EndZ=0
    g77: GeomPoint [constr] X=-30.5233 Y=-19.158 Z=0
    g78: GeomPoint [constr] X=-32.1423 Y=-16.2964 Z=0
    g79: Ellipse CenterX=-31.0799 CenterY=-9.50208 CenterZ=0 NormalX=0 NormalY=0 NormalZ=1 MajorRadius=2.385 MinorRadius=1.46 AngleXU=-1.27409
    g80: LineSegment [constr] StartX=-30.3826 StartY=-11.7829 StartZ=0 EndX=-31.7772 EndY=-7.22129 EndZ=0
    g81: LineSegment [constr] StartX=-29.6837 StartY=-9.07522 StartZ=0 EndX=-32.4761 EndY=-9.92894 EndZ=0
    g82: GeomPoint [constr] X=-30.5285 Y=-11.3056 Z=0
    g83: GeomPoint [constr] X=-31.6313 Y=-7.69858 Z=0
    g84: ArcOfCircle CenterX=-3.28958 CenterY=-16.1688 CenterZ=0 NormalX=0 NormalY=0 NormalZ=1 AngleXU=0 Radius=2.6 StartAngle=0.226445 EndAngle=2.51372
    g85: ArcOfCircle CenterX=-3.68832 CenterY=-18.1286 CenterZ=0 NormalX=0 NormalY=0 NormalZ=1 AngleXU=0 Radius=3.6 StartAngle=0.733279 EndAngle=2.00689
    g86: LineSegment [constr] StartX=-3.68832 StartY=-18.1286 StartZ=0 EndX=-3.28958 EndY=-16.1688 EndZ=0
    g87: ArcOfCircle CenterX=-29.978 CenterY=1.15 CenterZ=0 NormalX=0 NormalY=0 NormalZ=1 AngleXU=0 Radius=2.6 StartAngle=5.54097 EndAngle=7.82825
    g88: ArcOfCircle CenterX=-31.819 CenterY=0.368537 CenterZ=0 NormalX=0 NormalY=0 NormalZ=1 AngleXU=0 Radius=3.6 StartAngle=6.04781 EndAngle=7.32142
    g89: ArcOfCircle CenterX=35 CenterY=-0.610917 CenterZ=0 NormalX=0 NormalY=0 NormalZ=1 AngleXU=0 Radius=2.6 StartAngle=1.9805 EndAngle=4.26778
    g90: ArcOfCircle CenterX=36.9997 CenterY=-0.645821 CenterZ=0 NormalX=0 NormalY=0 NormalZ=1 AngleXU=0 Radius=3.6 StartAngle=2.48734 EndAngle=3.76094
    g91: LineSegment [constr] StartX=36.9997 StartY=-0.645821 StartZ=0 EndX=35 EndY=-0.610917 EndZ=0
    g92: ArcOfCircle CenterX=-23.1216 CenterY=-4.2 CenterZ=0 NormalX=0 NormalY=0 NormalZ=1 AngleXU=0 Radius=2.6 StartAngle=5.92494 EndAngle=8.21222
    g93: ArcOfCircle CenterX=-24.5358 CenterY=-5.61421 CenterZ=0 NormalX=0 NormalY=0 NormalZ=1 AngleXU=0 Radius=3.6 StartAngle=0.148594 EndAngle=1.4222
    g94: ArcOfCircle CenterX=-34.0259 CenterY=8.2 CenterZ=0 NormalX=0 NormalY=0 NormalZ=1 AngleXU=0 Radius=2.6 StartAngle=5.13955 EndAngle=7.42682
    g95: ArcOfCircle CenterX=-36.0259 CenterY=8.2 CenterZ=0 NormalX=0 NormalY=0 NormalZ=1 AngleXU=0 Radius=3.6 StartAngle=5.64638 EndAngle=6.91999
    g96: ArcOfCircle CenterX=30.0791 CenterY=-7.5 CenterZ=0 NormalX=0 NormalY=0 NormalZ=1 AngleXU=0 Radius=2.6 StartAngle=1.41327 EndAngle=3.70055
    g97: ArcOfCircle CenterX=31.7468 CenterY=-8.60387 CenterZ=0 NormalX=0 NormalY=0 NormalZ=1 AngleXU=0 Radius=3.6 StartAngle=1.9201 EndAngle=3.19371
    g98: ArcOfCircle CenterX=2.1086 CenterY=-21.8987 CenterZ=0 NormalX=0 NormalY=0 NormalZ=1 AngleXU=0 Radius=2.6 StartAngle=0.523151 EndAngle=2.81043
    g99: ArcOfCircle CenterX=2.30029 CenterY=-23.8895 CenterZ=0 NormalX=0 NormalY=0 NormalZ=1 AngleXU=0 Radius=3.6 StartAngle=1.02998 EndAngle=2.30359
    g100: LineSegment [constr] StartX=2.30029 StartY=-23.8895 StartZ=0 EndX=2.1086 EndY=-21.8987 EndZ=0
    g101: LineSegment StartX=8.04881 StartY=19 StartZ=0 EndX=4.79613 EndY=-7.49106 EndZ=0
    g102: ArcOfCircle CenterX=23.724 CenterY=-9.8151 CenterZ=0 NormalX=0 NormalY=0 NormalZ=1 AngleXU=0 Radius=19.07 StartAngle=3.01942 EndAngle=3.72139
    g103: ArcOfCircle CenterX=14.5718 CenterY=-15.8086 CenterZ=0 NormalX=0 NormalY=0 NormalZ=1 AngleXU=0 Radius=8.13 StartAngle=3.72139 EndAngle=5.53863
    g104: ArcOfCircle CenterX=6.15897 CenterY=-8.05635 CenterZ=0 NormalX=0 NormalY=0 NormalZ=1 AngleXU=0 Radius=19.57 StartAngle=5.53863 EndAngle=6.06966
    g105: ArcOfCircle CenterX=23.799 CenterY=-11.8813 CenterZ=0 NormalX=0 NormalY=0 NormalZ=1 AngleXU=0 Radius=1.52 StartAngle=6.06966 EndAngle=9.07368
    g106: ArcOfCircle CenterX=18.0242 CenterY=-9.76613 CenterZ=0 NormalX=0 NormalY=0 NormalZ=1 AngleXU=0 Radius=4.63 StartAngle=3.4029 EndAngle=5.93208
    g107: ArcOfCircle CenterX=41.6732 CenterY=-3.44186 CenterZ=0 NormalX=0 NormalY=0 NormalZ=1 AngleXU=0 Radius=29.11 StartAngle=3.02879 EndAngle=3.4029
    g108: LineSegment StartX=12.7482 StartY=-0.165091 StartZ=0 EndX=14.558 EndY=14.5742 EndZ=0
    g109: LineSegment StartX=19.5604 StartY=19 StartZ=0 EndX=25.5604 EndY=19 EndZ=0
    g110: ArcOfCircle CenterX=19.5604 CenterY=13.96 CenterZ=0 NormalX=0 NormalY=0 NormalZ=1 AngleXU=0 Radius=5.04 StartAngle=1.5708 EndAngle=3.01942
    g111: GeomPoint [constr] X=15.1014 Y=19 Z=0
    g112: ArcOfCircle CenterX=25.5604 CenterY=22.64 CenterZ=0 NormalX=0 NormalY=0 NormalZ=1 AngleXU=0 Radius=3.64 StartAngle=4.71239 EndAngle=6.58928
    g113: LineSegment [constr] StartX=0 StartY=-71.5751 StartZ=0 EndX=0 EndY=-50.0337 EndZ=0
    g114: ArcOfCircle CenterX=-40.9001 CenterY=-2.86001 CenterZ=0 NormalX=0 NormalY=0 NormalZ=1 AngleXU=0 Radius=8.38 StartAngle=0.030432 EndAngle=1.11467
    g115: ArcOfCircle CenterX=-33.8074 CenterY=-9.05865 CenterZ=0 NormalX=0 NormalY=0 NormalZ=1 AngleXU=0 Radius=6.58 StartAngle=6.20233 EndAngle=7.65768
    g116: ArcOfCircle CenterX=-27.2798 CenterY=-15.75 CenterZ=0 NormalX=0 NormalY=0 NormalZ=1 AngleXU=0 Radius=6.16 StartAngle=6.02684 EndAngle=7.84897
    g117: ArcOfCircle CenterX=-14.5498 CenterY=-19.0867 CenterZ=0 NormalX=0 NormalY=0 NormalZ=1 AngleXU=0 Radius=7 StartAngle=2.88525 EndAngle=5.39568
    g118: ArcOfCircle CenterX=-6.19075 CenterY=-29.3543 CenterZ=0 NormalX=0 NormalY=0 NormalZ=1 AngleXU=0 Radius=6.24 StartAngle=0.704991 EndAngle=2.25409
    g119: ArcOfCircle CenterX=1.96617 CenterY=-22.4139 CenterZ=0 NormalX=0 NormalY=0 NormalZ=1 AngleXU=0 Radius=4.47 StartAngle=3.84658 EndAngle=5.42057
    g120: ArcOfCircle CenterX=8.6984 CenterY=-30.2752 CenterZ=0 NormalX=0 NormalY=0 NormalZ=1 AngleXU=0 Radius=5.88 StartAngle=1.24712 EndAngle=2.27898
    g121: ArcOfCircle CenterX=14.5665 CenterY=-12.7833 CenterZ=0 NormalX=0 NormalY=0 NormalZ=1 AngleXU=0 Radius=12.57 StartAngle=4.38871 EndAngle=5.9264
    g122: ArcOfCircle CenterX=35.94 CenterY=-20.75 CenterZ=0 NormalX=0 NormalY=0 NormalZ=1 AngleXU=0 Radius=10.24 StartAngle=1.95984 EndAngle=2.78481
    g123: ArcOfCircle CenterX=37.8638 CenterY=-12.897 CenterZ=0 NormalX=0 NormalY=0 NormalZ=1 AngleXU=0 Radius=6.03 StartAngle=2.06124 EndAngle=2.86929
    g124: ArcOfCircle CenterX=32.8192 CenterY=-3.44945 CenterZ=0 NormalX=0 NormalY=0 NormalZ=1 AngleXU=0 Radius=4.68 StartAngle=5.20283 EndAngle=5.88136
    g125: ArcOfCircle CenterX=0 CenterY=1.33e-14 CenterZ=0 NormalX=0 NormalY=0 NormalZ=1 AngleXU=0 Radius=37.5 StartAngle=6.14192 EndAngle=6.96859
    g126: ArcOfCircle CenterX=-2.84e-14 CenterY=7.46e-14 CenterZ=0 NormalX=0 NormalY=0 NormalZ=1 AngleXU=0 Radius=37.5 StartAngle=0.843037 EndAngle=3.01692
    g127: LineSegment [constr] StartX=-40.9001 StartY=-2.86001 StartZ=0 EndX=0 EndY=1.33e-14 EndZ=0
    g128: LineSegment [constr] StartX=-27.2798 StartY=-15.75 StartZ=0 EndX=0 EndY=-1.8e-15 EndZ=0
    g129: LineSegment [constr] StartX=-14.5498 StartY=-19.0867 StartZ=0 EndX=0 EndY=0 EndZ=0
    g130: LineSegment [constr] StartX=-6.19075 StartY=-29.3543 StartZ=0 EndX=0 EndY=0 EndZ=0
    g131: LineSegment [constr] StartX=8.6984 StartY=-30.2752 StartZ=0 EndX=0 EndY=0 EndZ=0
    g132: LineSegment [constr] StartX=1.96617 StartY=-22.4139 StartZ=0 EndX=-2e-16 EndY=0 EndZ=0
    g133: LineSegment [constr] StartX=14.5718 StartY=-15.8086 StartZ=0 EndX=1.8e-15 EndY=0 EndZ=0
    g134: LineSegment [constr] StartX=35.94 StartY=-20.75 StartZ=0 EndX=0 EndY=0 EndZ=0
    g135: LineSegment [constr] StartX=37.8638 StartY=-12.897 StartZ=0 EndX=0 EndY=0 EndZ=0
    g136: LineSegment [constr] StartX=32.8192 StartY=-3.44945 StartZ=0 EndX=0 EndY=0 EndZ=0
    g137: LineSegment [constr] StartX=-33.8074 StartY=-9.05865 StartZ=0 EndX=0 EndY=0 EndZ=0
    g138: LineSegment [constr] StartX=23.799 StartY=-11.8813 StartZ=0 EndX=-2.84e-14 EndY=7.46e-14 EndZ=0
    g139: LineSegment [constr] StartX=18.0242 StartY=-9.76613 StartZ=0 EndX=0 EndY=0 EndZ=0
    g140: LineSegment [constr] StartX=-15.8813 StartY=12.82 StartZ=0 EndX=0 EndY=0 EndZ=0
    g141: LineSegment [constr] StartX=-25.5341 StartY=12.1792 StartZ=0 EndX=0 EndY=0 EndZ=0
    g142: LineSegment [constr] StartX=-10.8953 StartY=14 StartZ=0 EndX=0 EndY=0 EndZ=0
    g143: ArcOfCircle CenterX=30.4634 CenterY=-5.08034 CenterZ=0 NormalX=0 NormalY=0 NormalZ=1 AngleXU=0 Radius=0.15 StartAngle=5.0617 EndAngle=7.69645
    g144: ArcOfCircle CenterX=28.0019 CenterY=-8.79923 CenterZ=0 NormalX=0 NormalY=0 NormalZ=1 AngleXU=0 Radius=0.15 StartAngle=3.70055 EndAngle=6.3353
    g145: ArcOfCircle CenterX=33.9462 CenterY=-2.82272 CenterZ=0 NormalX=0 NormalY=0 NormalZ=1 AngleXU=0 Radius=0.15 StartAngle=4.26778 EndAngle=6.90254
    g146: ArcOfCircle CenterX=34.0241 CenterY=1.63632 CenterZ=0 NormalX=0 NormalY=0 NormalZ=1 AngleXU=0 Radius=0.15 StartAngle=5.62893 EndAngle=8.26369
    g147: ArcOfCircle CenterX=-0.20828 CenterY=-21.1021 CenterZ=0 NormalX=0 NormalY=0 NormalZ=1 AngleXU=0 Radius=0.15 StartAngle=2.81043 EndAngle=5.44519
    g148: ArcOfCircle CenterX=4.23091 CenterY=-20.6747 CenterZ=0 NormalX=0 NormalY=0 NormalZ=1 AngleXU=0 Radius=0.15 StartAngle=4.17158 EndAngle=6.80634
    g149: ArcOfCircle CenterX=-5.27231 CenterY=-14.7296 CenterZ=0 NormalX=0 NormalY=0 NormalZ=1 AngleXU=0 Radius=0.15 StartAngle=2.51372 EndAngle=5.14848
    g150: ArcOfCircle CenterX=-0.902125 CenterY=-15.6187 CenterZ=0 NormalX=0 NormalY=0 NormalZ=1 AngleXU=0 Radius=0.15 StartAngle=3.87487 EndAngle=6.50963
    g151: ArcOfCircle CenterX=-20.8272 CenterY=-5.05904 CenterZ=0 NormalX=0 NormalY=0 NormalZ=1 AngleXU=0 Radius=0.15 StartAngle=3.29019 EndAngle=5.92494
    g152: ArcOfCircle CenterX=-23.9807 CenterY=-1.90554 CenterZ=0 NormalX=0 NormalY=0 NormalZ=1 AngleXU=0 Radius=0.15 StartAngle=1.92904 EndAngle=4.5638
    g153: ArcOfCircle CenterX=-29.9149 CenterY=3.59919 CenterZ=0 NormalX=0 NormalY=0 NormalZ=1 AngleXU=0 Radius=0.15 StartAngle=1.54506 EndAngle=4.17982
    g154: ArcOfCircle CenterX=-28.1724 CenterY=-0.506004 CenterZ=0 NormalX=0 NormalY=0 NormalZ=1 AngleXU=0 Radius=0.15 StartAngle=2.90621 EndAngle=5.54097
    g155: ArcOfCircle CenterX=-33.0109 CenterY=5.97014 CenterZ=0 NormalX=0 NormalY=0 NormalZ=1 AngleXU=0 Radius=0.15 StartAngle=2.50479 EndAngle=5.13955
    g156: ArcOfCircle CenterX=-33.0109 CenterY=10.4299 CenterZ=0 NormalX=0 NormalY=0 NormalZ=1 AngleXU=0 Radius=0.15 StartAngle=1.14364 EndAngle=3.7784
    g157: LineSegment [constr] StartX=-36.0259 StartY=8.2 StartZ=0 EndX=-34.0259 EndY=8.2 EndZ=0
    g158: LineSegment [constr] StartX=-31.819 StartY=0.368537 StartZ=0 EndX=-29.978 EndY=1.15 EndZ=0
    g159: LineSegment [constr] StartX=-24.5358 StartY=-5.61421 StartZ=0 EndX=-23.1216 EndY=-4.2 EndZ=0
    g160: LineSegment [constr] StartX=30.0791 StartY=-7.5 StartZ=0 EndX=31.7468 EndY=-8.60387 EndZ=0
  constraints (338):
    c: Diameter(g0) = 82
    c: Coincident(g1,g0)
    c: Diameter(g1) = 75
    c: PointOnObject(g2,g1)
    c: Horizontal(g2)
    c: PointOnObject(g5,g3)
    c: PointOnObject(g5,g2)
    c: Tangent(g3,g4) = -1.5708
    c: Tangent(g2,g4) = -1.5708
    c: Distance(g0,g2) = 28
    c: Radius(g4) = 14
    c: Coincident(g6,g3)
    c: Coincident(g7,g6)
    c: Horizontal(g8)
    c: PointOnObject(g10,g7)
    c: PointOnObject(g10,g8)
    c: Tangent(g7,g9) = 1.5708
    c: Tangent(g8,g9) = 1.5708
    c: Distance(g2,g8) = 9
    c: Coincident(g11,g8)
    c: PointOnObject(g14,g12)
    c: PointOnObject(g14,g11)
    c: Tangent(g12,g13) = -1.5708
    c: Tangent(g11,g13) = 1.5708
    c: DistanceX(g8,g0) = 10.5
    c: Tangent(g16,g15) = -1.5708
    c: Tangent(g15,g12) = 1.5708
    c: Coincident(g18,g17)
    c: Horizontal(g18)
    c: Tangent(g17,g16) = -1.5708
    c: Parallel(g11,g17)
    c: Angle(g17,g18) = 1.69297
    c: PointOnObject(g8,g18)
    c: Distance(g17,g11) = 6.5
    c: InternalAlignment(g20-g23 -> g19) x4
    c: InternalAlignment(g25-g28 -> g24) x4
    c: InternalAlignment(g30-g33 -> g29) x4
    c: InternalAlignment(g35-g38 -> g34) x4
    c: InternalAlignment(g40-g43 -> g39) x4
    c: InternalAlignment(g45-g48 -> g44) x4
    c: InternalAlignment(g50-g53 -> g49) x4
    c: InternalAlignment(g55-g58 -> g54) x4
    c: InternalAlignment(g60-g63 -> g59) x4
    c: InternalAlignment(g65-g68 -> g64) x4
    c: InternalAlignment(g70-g73 -> g69) x4
    c: InternalAlignment(g75-g78 -> g74) x4
    c: InternalAlignment(g80-g83 -> g79) x4
    c: Coincident(g86,g85)
    c: Coincident(g86,g84)
    c: Radius(g85) = 3.6
    c: Radius(g84) = 2.6
    c: Distance(g86,g86) = 2
    c: Radius(g88) = 3.6
    c: Radius(g87) = 2.6
    c: Distance(g88,g87) = 2
    c: Coincident(g91,g90)
    c: Coincident(g91,g89)
    c: Radius(g90) = 3.6
    c: Radius(g89) = 2.6
    c: Distance(g91,g91) = 2
    c: Radius(g93) = 3.6
    c: Radius(g92) = 2.6
    c: Distance(g93,g92) = 2
    c: Radius(g95) = 3.6
    c: Radius(g94) = 2.6
    c: Distance(g95,g94) = 2
    c: Radius(g97) = 3.6
    c: Radius(g96) = 2.6
    c: Distance(g97,g96) = 2
    c: Coincident(g100,g99)
    c: Coincident(g100,g98)
    c: Radius(g99) = 3.6
    c: Radius(g98) = 2.6
    c: Distance(g100,g100) = 2
    c: Coincident(g101,g18)
    c: Tangent(g102,g101) = -1.5708
    c: Parallel(g17,g101)
    c: DistanceX(g18,g18) = 12
    c: Tangent(g103,g102) = -1.5708
    c: Tangent(g104,g103) = -1.5708
    c: Tangent(g105,g104) = -1.5708
    c: Tangent(g106,g105) = 1.5708
    c: Tangent(g107,g106) = -1.5708
    c: Coincident(g108,g107)
    c: Parallel(g101,g108)
    c: Horizontal(g109)
    c: PointOnObject(g109,g18)
    c: PointOnObject(g111,g108)
    c: PointOnObject(g111,g109)
    c: Tangent(g108,g110) = 1.5708
    c: Tangent(g109,g110) = 1.5708
    c: Tangent(g112,g109) = -1.5708
    c: PointOnObject(g112,g1)
    c: Vertical(g113)
    c: PointOnObject(g0,g113)
    c: PointOnObject(g114,g1)
    c: Coincident(g115,g114)
    c: Coincident(g116,g115)
    c: Coincident(g123,g122)
    c: PointOnObject(g124,g1)
    c: Tangent(g119,g118) = 1.5708
    c: Tangent(g120,g119) = 1.5708
    c: Tangent(g121,g120) = 1.5708
    c: Tangent(g122,g121) = 1.5708
    c: Tangent(g124,g123) = 1.5708
    c: Tangent(g118,g117) = 1.5708
    c: Tangent(g117,g116) = 1.5708
    c: Coincident(g125,g112)
    c: Coincident(g125,g124)
    c: Coincident(g126,g2)
    c: Coincident(g126,g114)
    c: Radius(g125) = 37.5
    c: Angle(g4) = 1.18141
    c: Radius(g6) = 1.16
    c: Radius(g9) = 6.18
    c: Radius(g13) = 18.54
    c: Radius(g15) = 5.39
    c: Radius(g102) = 19.07
    c: Radius(g103) = 8.13
    c: Radius(g104) = 19.57
    c: Radius(g105) = 1.52
    c: Radius(g106) = 4.63
    c: Radius(g107) = 29.11
    c: Radius(g110) = 5.04
    c: Radius(g112) = 3.64
    c: DistanceX(g109,g109) = 6
    c: Distance(g108,g108) = 14.85
    c: Distance(g101,g101) = 26.69
    c: Distance(g17,g17) = 36.83
    c: Distance(g11,g11) = 21.46
    c: Distance(g108,g101) = 7
    c: Radius(g124) = 4.68
    c: Radius(g123) = 6.03
    c: Radius(g122) = 10.24
    c: Radius(g121) = 12.57
    c: Radius(g120) = 5.88
    c: Radius(g119) = 4.47
    c: Radius(g118) = 6.24
    c: Radius(g117) = 7
    c: Radius(g116) = 6.16
    c: Radius(g115) = 6.58
    c: Radius(g114) = 8.38
    c: Distance(g80,g80) = 4.77
    c: Distance(g81,g81) = 2.92
    c: PointOnObject(g125,g86)
    c: PointOnObject(g125,g100)
    c: PointOnObject(g125,g91)
    c: PointOnObject(g125,g51)
    c: PointOnObject(g125,g46)
    c: PointOnObject(g125,g26)
    c: PointOnObject(g125,g31)
    c: PointOnObject(g125,g36)
    c: PointOnObject(g125,g41)
    c: PointOnObject(g125,g21)
    c: PointOnObject(g125,g56)
    c: PointOnObject(g125,g61)
    c: PointOnObject(g125,g71)
    c: PointOnObject(g125,g76)
    c: PointOnObject(g125,g81)
    c: PointOnObject(g125,g66)
    c: Distance(g84,g125) = 16.5
    c: Distance(g98,g125) = 22
    c: Distance(g96,g125) = 31
    c: DistanceX(g125,g89) = 35
    c: Distance(g92,g125) = 23.5
    c: Distance(g87,g125) = 30
    c: Distance(g94,g125) = 35
    c: Distance(g64,g125) = 36
    c: Distance(g79,g125) = 32.5
    c: Distance(g69,g125) = 30.5
    c: Distance(g74,g125) = 36
    c: Distance(g59,g125) = 36
    c: Distance(g54,g125) = 36
    c: Distance(g44,g125) = 36
    c: Distance(g29,g125) = 36
    c: Distance(g34,g125) = 36
    c: Distance(g39,g125) = 34.5
    c: Distance(g19,g125) = 36
    c: Angle(g-1,g86) = 1.37008
    c: Angle(g-1,g100) = 1.66679
    c: Angle(g91,g-1) = 0.017453
    c: Angle(g-1,g66) = 0.061087
    c: Angle(g-1,g81) = 0.296706
    c: Angle(g-1,g71) = 0.575959
    c: Angle(g-1,g76) = 0.514872
    c: Angle(g-1,g61) = 0.750492
    c: Angle(g-1,g56) = 1.06465
    c: Angle(g-1,g51) = 1.28282
    c: Angle(g-1,g46) = 1.52716
    c: Angle(g-1,g26) = 1.78024
    c: Angle(g-1,g31) = 1.95477
    c: Angle(g-1,g36) = 2.21657
    c: Angle(g-1,g41) = 2.56563
    c: Angle(g-1,g21) = 2.80998
    c: Distance(g20,g20) = 4.5
    c: Distance(g21,g21) = 1.2
    c: Distance(g40,g40) = 4
    c: Distance(g41,g41) = 2.2
    c: Distance(g35,g35) = 3.75
    c: Distance(g36,g36) = 2.3
    c: Distance(g30,g30) = 4.1
    c: Distance(g31,g31) = 2.3
    c: Distance(g25,g25) = 4.2
    c: Distance(g26,g26) = 2.8
    c: Distance(g24,g125) = 30.5
    c: DistanceX(g45,g45) = 5
    c: DistanceY(g46,g46) = 2.6
    c: Distance(g51,g51) = 3
    c: Distance(g50,g50) = 4.5
    c: Distance(g49,g125) = 30
    c: Distance(g55,g55) = 4.3
    c: Distance(g56,g56) = 2
    c: Distance(g60,g60) = 4.3
    c: Distance(g61,g61) = 1.8
    c: Distance(g70,g70) = 5
    c: Distance(g71,g71) = 3.1
    c: Distance(g75,g75) = 3.5
    c: Distance(g76,g76) = 1.2
    c: DistanceX(g66,g66) = 1.2
    c: DistanceY(g65,g65) = 4.9
    c: Distance(g114,g125) = 41
    c: Coincident(g127,g114)
    c: Coincident(g127,g125)
    c: Coincident(g128,g116)
    c: Coincident(g128,g0)
    c: Coincident(g129,g117)
    c: Coincident(g129,g0)
    c: Coincident(g130,g118)
    c: Coincident(g130,g0)
    c: Coincident(g131,g120)
    c: Coincident(g131,g0)
    c: Coincident(g132,g119)
    c: Coincident(g132,g0)
    c: Coincident(g133,g103)
    c: Coincident(g133,g0)
    c: Coincident(g134,g122)
    c: Coincident(g134,g0)
    c: Coincident(g135,g123)
    c: Coincident(g135,g0)
    c: Coincident(g136,g124)
    c: Coincident(g136,g0)
    c: Distance(g136,g136) = 33
    c: Distance(g135,g135) = 40
    c: Distance(g134,g134) = 41.5
    c: Distance(g133,g133) = 21.5
    c: Distance(g131,g131) = 31.5
    c: Distance(g132,g132) = 22.5
    c: Distance(g130,g130) = 30
    c: Distance(g129,g129) = 24
    c: Distance(g128,g128) = 31.5
    c: Distance(g115,g126) = 35
    c: Angle(g-1,g127) = 0.069813
    c: Angle(g-1,g128) = 0.523599
    c: Coincident(g137,g115)
    c: Coincident(g137,g0)
    c: Distance(g137,g137) = 35
    c: Angle(g-1,g137) = 0.261799
    c: Angle(g136,g-1) = 0.10472
    c: Angle(g134,g-1) = 0.523599
    c: Coincident(g15,g117)
    c: Coincident(g138,g105)
    c: Coincident(g138,g126)
    c: Distance(g138,g138) = 26.6
    c: Angle(g-1,g138) = 2.67856
    c: Coincident(g139,g106)
    c: Coincident(g139,g0)
    c: Distance(g139,g139) = 20.5
    c: Coincident(g140,g9)
    c: Coincident(g140,g0)
    c: Coincident(g141,g6)
    c: Coincident(g141,g0)
    c: Coincident(g142,g4)
    c: Coincident(g142,g0)
    c: Distance(g142,g142) = 17.74
    c: Distance(g140,g140) = 20.41
    c: Distance(g141,g141) = 28.29
    c: Angle(g141,g-1) = 0.445059
    c: Angle(g7,g-1) = 2.21517
    c: PointOnObject(g-1,g113)
    c: PointOnObject(g0,g-1)
    c: Tangent(g96,g143) = -1.5708
    c: Tangent(g97,g143) = 1.5708
    c: Radius(g143) = 0.15
    c: Tangent(g96,g144) = -1.5708
    c: Tangent(g97,g144) = 1.5708
    c: Tangent(g89,g145) = -1.5708
    c: Tangent(g90,g145) = 1.5708
    c: Tangent(g89,g146) = -1.5708
    c: Tangent(g90,g146) = 1.5708
    c: Tangent(g98,g147) = -1.5708
    c: Tangent(g99,g147) = 1.5708
    c: Tangent(g99,g148) = 1.5708
    c: Tangent(g98,g148) = -1.5708
    c: Tangent(g84,g149) = -1.5708
    c: Tangent(g85,g149) = 1.5708
    c: Tangent(g85,g150) = 1.5708
    c: Tangent(g84,g150) = -1.5708
    c: Tangent(g93,g151) = 1.5708
    c: Tangent(g92,g151) = -1.5708
    c: Tangent(g93,g152) = 1.5708
    c: Tangent(g92,g152) = -1.5708
    c: Tangent(g88,g153) = 1.5708
    c: Tangent(g87,g153) = -1.5708
    c: Tangent(g88,g154) = 1.5708
    c: Tangent(g87,g154) = -1.5708
    c: Tangent(g95,g155) = 1.5708
    c: Tangent(g94,g155) = -1.5708
    c: Tangent(g95,g156) = 1.5708
    c: Tangent(g94,g156) = -1.5708
    c: Radius(g156) = 0.15
    c: Radius(g155) = 0.15
    c: Radius(g153) = 0.15
    c: Radius(g154) = 0.15
    c: Radius(g152) = 0.15
    c: Radius(g151) = 0.15
    c: Radius(g149) = 0.15
    c: Radius(g150) = 0.15
    c: Radius(g147) = 0.15
    c: Radius(g148) = 0.15
    c: Radius(g144) = 0.15
    c: Radius(g145) = 0.15
    c: Radius(g146) = 0.15
    c: Coincident(g157,g95)
    c: Coincident(g157,g94)
    c: Coincident(g158,g88)
    c: Coincident(g158,g87)
    c: Coincident(g159,g93)
    c: Coincident(g159,g92)
    c: Coincident(g160,g96)
    c: Coincident(g160,g97)
    c: Horizontal(g157)
    c: Distance(g94,g-1) = 8.2
    c: Distance(g87,g-1) = 1.15
    c: Angle(g-1,g158) = 0.401426
    c: Distance(g92,g-1) = 4.2
    c: Angle(g-1,g159) = 0.785398
    c: Distance(g96,g-1) = 7.5
    c: Angle(g160,g-1) = 0.584685
FEATURE [PartDesign::Pad] Pad
  Direction = (0,0,1)
  Length = 3
  Length2 = 10
  Profile = -> Sketch
  ReferenceAxis = -> Sketch [N_Axis]
  Refine = true
  Suppressed = false
  Type = 0
FEATURE [PartDesign::ShapeBinder] CopyScale
  TraceSupport = false
FEATURE [Sketcher::SketchObject] Sketch001
  ArcFitTolerance = 1e-06
  AttachmentSupport = -> [CopyScale]
  FullyConstrained = true
  MakeInternals = false
  MapMode = 5
  Placement = pos=(0,0,0) rot=(1,0,0;3.14159rad)
  sketch-geometry (10):
    g0: Circle CenterX=0 CenterY=-23.23 CenterZ=0 NormalX=0 NormalY=0 NormalZ=1 AngleXU=0 Radius=2.75
    g1: Circle CenterX=-13.9802 CenterY=18.5523 CenterZ=0 NormalX=0 NormalY=0 NormalZ=1 AngleXU=0 Radius=2.75
    g2: Circle CenterX=13.3242 CenterY=19.0289 CenterZ=0 NormalX=0 NormalY=0 NormalZ=1 AngleXU=0 Radius=2.75
    g3: LineSegment [constr] StartX=13.3242 StartY=19.0289 StartZ=0 EndX=0 EndY=0 EndZ=0
    g4: LineSegment [constr] StartX=-13.9802 StartY=18.5523 StartZ=0 EndX=1.8e-15 EndY=0 EndZ=0
    g5: Circle CenterX=-13.9802 CenterY=18.5523 CenterZ=0 NormalX=0 NormalY=0 NormalZ=1 AngleXU=0 Radius=1.25
    g6: Circle CenterX=13.3242 CenterY=19.0289 CenterZ=0 NormalX=0 NormalY=0 NormalZ=1 AngleXU=0 Radius=1.25
    g7: Circle CenterX=0 CenterY=-23.23 CenterZ=0 NormalX=0 NormalY=0 NormalZ=1 AngleXU=0 Radius=1.25
    g8: Circle CenterX=0 CenterY=30.8 CenterZ=0 NormalX=0 NormalY=0 NormalZ=1 AngleXU=0 Radius=2.75
    g9: Circle CenterX=0 CenterY=30.8 CenterZ=0 NormalX=0 NormalY=0 NormalZ=1 AngleXU=0 Radius=1.25
  constraints (24):
    c: PointOnObject(g0,g-2)
    c: Coincident(g3,g2)
    c: Coincident(g3,g-1)
    c: Coincident(g4,g1)
    c: Coincident(g4,g3)
    c: Distance(g4,g4) = 23.23
    c: DistanceY(g0,g-1) = 23.23
    c: Diameter(g0) = 5.5
    c: Diameter(g1) = 5.5
    c: Diameter(g2) = 5.5
    c: Angle(g3,g-2) = 0.610865
    c: Angle(g-2,g4) = 0.645772
    c: Distance(g3,g3) = 23.23
    c: Coincident(g5,g1)
    c: Diameter(g5) = 2.5
    c: Coincident(g6,g2)
    c: Coincident(g7,g0)
    c: Diameter(g7) = 2.5
    c: Diameter(g6) = 2.5
    c: PointOnObject(g8,g-2)
    c: Diameter(g8) = 5.5
    c: Coincident(g9,g8)
    c: Diameter(g9) = 2.5
    c: Distance(g8,g-1) = 30.8
FEATURE [PartDesign::Pad] Pad001
  BaseFeature = -> Pad
  Direction = (0,0,-1)
  Length = 9
  Length2 = 10
  Profile = -> Sketch001
  ReferenceAxis = -> Sketch001 [N_Axis]
  Refine = true
  Suppressed = false
  Type = 0
FEATURE [PartDesign::Body] Body  label="Stack_Module_Cover_LogoBall001"
  AllowCompound = false
  Group = -> [Sketch,Pad,CopyScale,Sketch001,Pad001]
  Origin = -> Origin001
  Tip = -> Pad001
FEATURE [Part::Scale] Scale
  Base = -> Body
  Uniform = false
  UniformScale = 1
  XScale = 0.99
  YScale = 0.99
  ZScale = 1
FEATURE [PartDesign::CoordinateSystem] LCS_1
  AttacherType = Attacher::AttachEngine3D
  AttachmentSupport = -> [Scale]
  MapMode = 11
  Placement = pos=(-7.1e-15,0,0) rot=(0,0,1;1.5708rad)
FEATURE [App::Part] Part  label="Stack_Module_Cover_LogoBall"
  Group = -> [Body,Scale,LCS_1]
  Origin = -> Origin
---- part ../../Part/Print/Stack_Module_Cover_LogoTee.FCStd = doc fcstd_482eb0057cc3 ----
FCSTD DOCUMENT  (FreeCAD 1.0R39319 (Git))
Label: Stack_Module_Cover_LogoTee
License: All rights reserved
LicenseURL: https://en.wikipedia.org/wiki/All_rights_reserved
objects: Sketcher::SketchObject×3, PartDesign::Pad×2, PartDesign::Body×2, Part::Scale×1, PartDesign::FeatureBase×1, PartDesign::Pocket×1, PartDesign::Chamfer×1, PartDesign::CoordinateSystem×1, App::Part×1
note: 24 computed .brp shape members not serialized (recipe doc carries the construction recipe); baked Part::Feature solids carry a one-line shape summary decoded from their .brp

FEATURE [Sketcher::SketchObject] Sketch
  ArcFitTolerance = 1e-06
  AttachmentSupport = -> [XY_Plane001]
  FullyConstrained = false
  MakeInternals = false
  MapMode = 5
  sketch-geometry (15):
    g0: ArcOfCircle CenterX=0 CenterY=0 CenterZ=0 NormalX=0 NormalY=0 NormalZ=1 AngleXU=0 Radius=44 StartAngle=4.3176 EndAngle=5.10718
    g1: ArcOfCircle CenterX=22 CenterY=-62.5913 CenterZ=0 NormalX=0 NormalY=0 NormalZ=1 AngleXU=0 Radius=18 StartAngle=2.17527 EndAngle=2.9376
    g2: ArcOfCircle CenterX=-22 CenterY=-62.5913 CenterZ=0 NormalX=0 NormalY=0 NormalZ=1 AngleXU=0 Radius=18 StartAngle=0.20399 EndAngle=0.966323
    g3: LineSegment StartX=-4.37321 StartY=-58.9449 StartZ=0 EndX=-2.66496 EndY=-67.2026 EndZ=0
    g4: LineSegment StartX=-1.68569 StartY=-68 StartZ=0 EndX=1.68569 EndY=-68 EndZ=0
    g5: LineSegment StartX=2.66496 StartY=-67.2026 StartZ=0 EndX=4.37321 EndY=-58.9449 EndZ=0
    g6: LineSegment [constr] StartX=0 StartY=-68 StartZ=0 EndX=0 EndY=-44 EndZ=0
    g7: ArcOfCircle CenterX=1.68569 CenterY=-67 CenterZ=0 NormalX=0 NormalY=0 NormalZ=1 AngleXU=0 Radius=1 StartAngle=4.71239 EndAngle=6.0792
    g8: GeomPoint [constr] X=2.5 Y=-68 Z=0
    g9: ArcOfCircle CenterX=-1.68569 CenterY=-67 CenterZ=0 NormalX=0 NormalY=0 NormalZ=1 AngleXU=0 Radius=1 StartAngle=3.34558 EndAngle=4.71239
    g10: GeomPoint [constr] X=-2.5 Y=-68 Z=0
    g11: LineSegment StartX=11.7701 StartY=-47.7808 StartZ=0 EndX=18.3525 EndY=-43.2342 EndZ=0
    g12: ArcOfCircle CenterX=17.5 CenterY=-42 CenterZ=0 NormalX=0 NormalY=0 NormalZ=1 AngleXU=0 Radius=1.5 StartAngle=5.31686 EndAngle=8.24877
    g13: LineSegment StartX=-11.7701 StartY=-47.7808 StartZ=0 EndX=-18.3525 EndY=-43.2342 EndZ=0
    g14: ArcOfCircle CenterX=-17.5 CenterY=-42 CenterZ=0 NormalX=0 NormalY=0 NormalZ=1 AngleXU=0 Radius=1.5 StartAngle=1.17601 EndAngle=4.10792
  constraints (35):
    c: Tangent(g2,g3) = 1.5708
    c: Horizontal(g4)
    c: Tangent(g5,g1) = 1.5708
    c: Symmetric(g10,g8,g6)
    c: PointOnObject(g6,g0)
    c: Vertical(g6)
    c: Radius(g0) = 44
    c: Distance(g10,g8) = 5
    c: Radius(g2) = 18
    c: Radius(g1) = 18
    c: Distance(g2,g6) = 22
    c: Distance(g1,g6) = 22
    c: PointOnObject(g8,g4)
    c: PointOnObject(g8,g5)
    c: Tangent(g4,g7) = -1.5708
    c: Tangent(g5,g7) = -1.5708
    c: PointOnObject(g10,g3)
    c: PointOnObject(g10,g4)
    c: Tangent(g3,g9) = -1.5708
    c: Tangent(g4,g9) = -1.5708
    c: Radius(g9) = 1
    c: Radius(g7) = 1
    c: PointOnObject(g-1,g6)
    c: Tangent(g12,g0) = 1.5708
    c: Tangent(g12,g11) = -1.5708
    c: Tangent(g11,g1) = 1.5708
    c: Radius(g12) = 1.5
    c: Distance(g11,g11) = 8
    c: Distance(g12,g6) = 17.5
    c: Tangent(g13,g2) = -1.5708
    c: Tangent(g14,g0) = 1.5708
    c: Tangent(g14,g13) = 1.5708
    c: Radius(g14) = 1.5
    c: Distance(g13,g13) = 8
    c: Distance(g14,g6) = 17.5
FEATURE [PartDesign::Pad] Pad
  Direction = (0,0,1)
  Length = 3
  Length2 = 10
  Profile = -> Sketch
  ReferenceAxis = -> Sketch [N_Axis]
  Refine = true
  Suppressed = false
  Type = 0
FEATURE [PartDesign::Body] Body  label="Stack_Module_Cover_LogoTee001"
  AllowCompound = false
  Group = -> [Sketch,Pad]
  Origin = -> Origin001
  Tip = -> Pad
FEATURE [Part::Scale] Scale
  Base = -> Body
  Uniform = false
  UniformScale = 1
  XScale = 0.98
  YScale = 0.98
  ZScale = 1
FEATURE [PartDesign::FeatureBase] BaseFeature
  BaseFeature = -> Scale
  Suppressed = false
FEATURE [Sketcher::SketchObject] Sketch001
  ArcFitTolerance = 1e-06
  AttachmentSupport = -> [BaseFeature]
  ExternalGeometry = -> [BaseFeature]
  FullyConstrained = true
  MakeInternals = false
  MapMode = 5
  Placement = pos=(0,0,0) rot=(1,0,0;3.14159rad)
  sketch-geometry (1):
    g0: Circle CenterX=0 CenterY=51.94 CenterZ=0 NormalX=0 NormalY=0 NormalZ=1 AngleXU=0 Radius=2.75
  constraints (3):
    c: PointOnObject(g0,g-2)
    c: Diameter(g0) = 5.5
    c: DistanceY(g0,g-3) = 14.7
FEATURE [PartDesign::Pad] Pad001
  BaseFeature = -> BaseFeature
  Direction = (0,0,-1)
  Length = 5
  Length2 = 10
  Profile = -> Sketch001
  ReferenceAxis = -> Sketch001 [N_Axis]
  Refine = true
  Suppressed = false
  Type = 0
FEATURE [Sketcher::SketchObject] Sketch002
  ArcFitTolerance = 1e-06
  AttachmentSupport = -> [Pad001]
  ExternalGeometry = -> [Pad001]
  FullyConstrained = true
  MakeInternals = false
  MapMode = 5
  Placement = pos=(0,0,-5) rot=(1,0,0;3.14159rad)
  sketch-geometry (1):
    g0: Circle CenterX=0 CenterY=51.94 CenterZ=0 NormalX=0 NormalY=0 NormalZ=1 AngleXU=0 Radius=1.25
  constraints (2):
    c: Coincident(g0,g-3)
    c: Diameter(g0) = 2.5
FEATURE [PartDesign::Pocket] Pocket
  BaseFeature = -> Pad001
  Direction = (0,0,1)
  Length = 7
  Length2 = 5
  Profile = -> Sketch002
  ReferenceAxis = -> Sketch002 [N_Axis]
  Refine = true
  Suppressed = false
  Type = 0
FEATURE [PartDesign::Chamfer] Chamfer
  Angle = 45
  Base = -> Pocket [Edge16]
  BaseFeature = -> Pocket
  ChamferType = 0
  FlipDirection = false
  Refine = true
  Size = 0.5
  Size2 = 1
  SupportTransform = false
  Suppressed = false
  UseAllEdges = false
FEATURE [PartDesign::Body] Body001  label="Body"
  AllowCompound = false
  BaseFeature = -> Scale
  Group = -> [BaseFeature,Sketch001,Pad001,Sketch002,Pocket,Chamfer]
  Origin = -> Origin002
  Tip = -> Chamfer
FEATURE [PartDesign::CoordinateSystem] LCS_1
  AttacherType = Attacher::AttachEngine3D
  AttachmentSupport = -> [Chamfer]
  MapMode = 11
  Placement = pos=(0,-51.94,0) rot=(0.707107,-0.707107,0;3.14159rad)
FEATURE [App::Part] Part  label="Stack_Module_Cover_LogoTee"
  Group = -> [Scale,Body001,Body,LCS_1]
  Origin = -> Origin
---- part ../../Part/Print/Stack_Module_Cover_forInserts.FCStd = doc fcstd_79f655607396 ----
FCSTD DOCUMENT  (FreeCAD 1.0R39319 (Git))
Label: Stack_Module_Cover_forInserts
License: All rights reserved
LicenseURL: https://en.wikipedia.org/wiki/All_rights_reserved
objects: Sketcher::SketchObject×27, PartDesign::Pocket×19, PartDesign::Pad×7, PartDesign::CoordinateSystem×7, PartDesign::Fillet×6, PartDesign::PolarPattern×3, PartDesign::Chamfer×3, PartDesign::LinearPattern×2, PartDesign::Point×2, PartDesign::Mirrored×1, PartDesign::Line×1, PartDesign::Body×1, App::Part×1
note: 182 computed .brp shape members not serialized (recipe doc carries the construction recipe); baked Part::Feature solids carry a one-line shape summary decoded from their .brp

FEATURE [Sketcher::SketchObject] Sketch
  ArcFitTolerance = 1e-06
  AttachmentSupport = -> [XZ_Plane001]
  FullyConstrained = true
  MakeInternals = false
  MapMode = 5
  Placement = pos=(0,0,0) rot=(1,0,0;1.5708rad)
  sketch-geometry (9):
    g0: LineSegment StartX=0 StartY=-70 StartZ=0 EndX=74 EndY=-70 EndZ=0
    g1: LineSegment StartX=74 StartY=-70 StartZ=0 EndX=74 EndY=-53.5 EndZ=0
    g2: ArcOfCircle CenterX=66.5 CenterY=-53.5 CenterZ=0 NormalX=0 NormalY=0 NormalZ=1 AngleXU=0 Radius=7.5 StartAngle=0 EndAngle=1.5708
    g3: ArcOfCircle CenterX=66.5 CenterY=-38.5 CenterZ=0 NormalX=0 NormalY=0 NormalZ=1 AngleXU=0 Radius=7.5 StartAngle=3.14159 EndAngle=4.71239
    g4: LineSegment StartX=59 StartY=-38.5 StartZ=0 EndX=59 EndY=47.8031 EndZ=0
    g5: ArcOfCircle CenterX=66.5 CenterY=47.8031 CenterZ=0 NormalX=0 NormalY=0 NormalZ=1 AngleXU=0 Radius=7.5 StartAngle=1.77215 EndAngle=3.14159
    g6: ArcOfCircle CenterX=63.5 CenterY=62.5 CenterZ=0 NormalX=0 NormalY=0 NormalZ=1 AngleXU=0 Radius=7.5 StartAngle=4.91375 EndAngle=7.85398
    g7: LineSegment StartX=63.5 StartY=70 StartZ=0 EndX=0 EndY=70 EndZ=0
    g8: LineSegment StartX=0 StartY=70 StartZ=0 EndX=0 EndY=-70 EndZ=0
  constraints (26):
    c: PointOnObject(g0,g-2)
    c: Horizontal(g0)
    c: Coincident(g0,g1)
    c: Vertical(g1)
    c: Tangent(g1,g2) = -1.5708
    c: Tangent(g2,g3) = 1.5708
    c: Tangent(g3,g4) = 1.5708
    c: Tangent(g4,g5) = 1.5708
    c: Tangent(g5,g6) = 1.5708
    c: Tangent(g6,g7) = -1.5708
    c: Coincident(g7,g8)
    c: Coincident(g8,g0)
    c: Vertical(g8)
    c: Horizontal(g7)
    c: Vertical(g4)
    c: DistanceX(g0,g0) = 74
    c: Distance(g7,g0) = 140
    c: Distance(g2,g0) = 16.5
    c: Radius(g2) = 7.5
    c: Distance(g8,g4) = 59
    c: Radius(g6) = 7.5
    c: Distance(g6,g8) = 63.5
    c: Distance(g2,g8) = 66.5
    c: Distance(g-1,g0) = 70
    c: Radius(g3) = 7.5
    c: Radius(g5) = 7.5
FEATURE [PartDesign::Pad] Pad
  Direction = (0,-1,2e-16)
  Length = 10
  Length2 = 10
  Placement = pos=(0,0,0) rot=(1,0,0;1.5708rad)
  Profile = -> Sketch
  ReferenceAxis = -> Sketch [N_Axis]
  Refine = true
  Suppressed = false
  Type = 0
FEATURE [PartDesign::Fillet] Fillet
  Base = -> Pad [Edge2]
  BaseFeature = -> Pad
  Placement = pos=(0,0,0) rot=(1,0,0;1.5708rad)
  Radius = 3
  Refine = true
  SupportTransform = false
  Suppressed = false
  UseAllEdges = false
FEATURE [Sketcher::SketchObject] Sketch001
  ArcFitTolerance = 1e-06
  AttachmentSupport = -> [YZ_Plane001]
  ExternalGeometry = -> [Fillet]
  FullyConstrained = true
  MakeInternals = false
  MapMode = 5
  Placement = pos=(0,0,0) rot=(0.57735,0.57735,0.57735;2.0944rad)
  sketch-geometry (5):
    g0: LineSegment StartX=-10 StartY=70 StartZ=0 EndX=-32 EndY=70 EndZ=0
    g1: LineSegment StartX=-32 StartY=70 StartZ=0 EndX=-32 EndY=56.275 EndZ=0
    g2: LineSegment StartX=-32 StartY=56.275 StartZ=0 EndX=-12 EndY=-70 EndZ=0
    g3: LineSegment StartX=-12 StartY=-70 StartZ=0 EndX=-10 EndY=-70 EndZ=0
    g4: LineSegment StartX=-10 StartY=-70 StartZ=0 EndX=-10 EndY=70 EndZ=0
  constraints (13):
    c: Horizontal(g0)
    c: Coincident(g0,g1)
    c: Vertical(g1)
    c: Coincident(g1,g2)
    c: Coincident(g2,g3)
    c: Horizontal(g3)
    c: Coincident(g3,g4)
    c: Coincident(g4,g0)
    c: Coincident(g0,g-3)
    c: Coincident(g3,g-5)
    c: Distance(g3,g3) = 2
    c: Angle(g4,g2) = 0.15708
    c: Distance(g-2,g1) = 32
FEATURE [PartDesign::Pad] Pad001
  BaseFeature = -> Fillet
  Direction = (1,0,0)
  Length = 50
  Length2 = 10
  Placement = pos=(0,0,0) rot=(1,0,0;1.5708rad)
  Profile = -> Sketch001
  ReferenceAxis = -> Sketch001 [N_Axis]
  Refine = true
  Suppressed = false
  Type = 0
FEATURE [Sketcher::SketchObject] Sketch002
  ArcFitTolerance = 1e-06
  AttachmentSupport = -> [Pad001]
  FullyConstrained = true
  MakeInternals = false
  MapMode = 5
  Placement = pos=(0,0,0) rot=(0.707107,0,-0.707107;3.14159rad)
FEATURE [Sketcher::SketchObject] Sketch003
  ArcFitTolerance = 1e-06
  AttachmentSupport = -> [Pad001]
  ExternalGeometry = -> [Pad001]
  FullyConstrained = true
  MakeInternals = false
  MapMode = 5
  Placement = pos=(0,-3e-16,0) rot=(-1,0,0;1.5708rad)
  sketch-geometry (4):
    g0: LineSegment StartX=0 StartY=67 StartZ=0 EndX=0 EndY=60 EndZ=0
    g1: LineSegment StartX=0 StartY=60 StartZ=0 EndX=71 EndY=60 EndZ=0
    g2: LineSegment StartX=71 StartY=60 StartZ=0 EndX=71 EndY=67 EndZ=0
    g3: LineSegment StartX=71 StartY=67 StartZ=0 EndX=0 EndY=67 EndZ=0
  constraints (12):
    c: Coincident(g0,g1)
    c: Coincident(g1,g2)
    c: Coincident(g2,g3)
    c: Coincident(g3,g0)
    c: Vertical(g0)
    c: Vertical(g2)
    c: Horizontal(g1)
    c: Horizontal(g3)
    c: PointOnObject(g0,g-2)
    c: Distance(g-3,g3) = 3
    c: Distance(g3,g1) = 7
    c: Distance(g-4,g2) = 3
FEATURE [PartDesign::Pocket] Pocket
  BaseFeature = -> Pad001
  Direction = (0,-1,-2e-16)
  Length = 3
  Length2 = 5
  Placement = pos=(0,0,0) rot=(1,0,0;1.5708rad)
  Profile = -> Sketch003
  ReferenceAxis = -> Sketch003 [N_Axis]
  Refine = true
  Suppressed = false
  Type = 0
FEATURE [Sketcher::SketchObject] Sketch004
  ArcFitTolerance = 1e-06
  AttachmentSupport = -> [Pocket]
  ExternalGeometry = -> [Pocket]
  FullyConstrained = true
  MakeInternals = false
  MapMode = 5
  Placement = pos=(0,-3e-16,0) rot=(-1,0,0;1.5708rad)
  sketch-geometry (4):
    g0: LineSegment StartX=0 StartY=-63.5 StartZ=0 EndX=0 EndY=-67 EndZ=0
    g1: LineSegment StartX=0 StartY=-67 StartZ=0 EndX=56 EndY=-67 EndZ=0
    g2: LineSegment StartX=56 StartY=-67 StartZ=0 EndX=56 EndY=-63.5 EndZ=0
    g3: LineSegment StartX=56 StartY=-63.5 StartZ=0 EndX=0 EndY=-63.5 EndZ=0
  constraints (12):
    c: Coincident(g0,g1)
    c: Coincident(g1,g2)
    c: Coincident(g2,g3)
    c: Coincident(g3,g0)
    c: Vertical(g0)
    c: Vertical(g2)
    c: Horizontal(g1)
    c: Horizontal(g3)
    c: PointOnObject(g0,g-2)
    c: Distance(g-2,g2) = 56
    c: Distance(g3,g1) = 3.5
    c: Distance(g-3,g1) = 3
FEATURE [PartDesign::Pocket] Pocket001
  BaseFeature = -> Pocket
  Direction = (0,-1,-2e-16)
  Length = 3
  Length2 = 5
  Placement = pos=(0,0,0) rot=(1,0,0;1.5708rad)
  Profile = -> Sketch004
  ReferenceAxis = -> Sketch004 [N_Axis]
  Refine = true
  Suppressed = false
  Type = 0
FEATURE [Sketcher::SketchObject] Sketch005
  ArcFitTolerance = 1e-06
  AttachmentSupport = -> [Pocket001]
  ExternalGeometry = -> [Pocket001]
  FullyConstrained = true
  MakeInternals = false
  MapMode = 5
  Placement = pos=(0,0,0) rot=(0.707107,0,-0.707107;3.14159rad)
  sketch-geometry (10):
    g0: LineSegment StartX=-43.4641 StartY=6 StartZ=0 EndX=-70 EndY=6 EndZ=0
    g1: LineSegment StartX=-70 StartY=6 StartZ=0 EndX=-70 EndY=26 EndZ=0
    g2: LineSegment StartX=-70 StartY=26 StartZ=0 EndX=-64 EndY=26 EndZ=0
    g3: LineSegment StartX=-64 StartY=26 StartZ=0 EndX=-64 EndY=30.1861 EndZ=0
    g4: LineSegment StartX=-64 StartY=30.1861 StartZ=0 EndX=57 EndY=11.0216 EndZ=0
    g5: LineSegment StartX=57 StartY=11.0216 StartZ=0 EndX=57 EndY=0 EndZ=0
    g6: LineSegment StartX=57 StartY=0 StartZ=0 EndX=-34 EndY=0 EndZ=0
    g7: LineSegment StartX=-43.4641 StartY=6 StartZ=0 EndX=-40 EndY=12 EndZ=0
    g8: LineSegment StartX=-40 StartY=12 StartZ=0 EndX=-34 EndY=12 EndZ=0
    g9: LineSegment StartX=-34 StartY=12 StartZ=0 EndX=-34 EndY=0 EndZ=0
  constraints (30):
    c: PointOnObject(g6,g-1)
    c: Horizontal(g0)
    c: Coincident(g0,g1)
    c: Vertical(g1)
    c: Coincident(g1,g2)
    c: Horizontal(g2)
    c: Coincident(g2,g3)
    c: Vertical(g3)
    c: Coincident(g3,g4)
    c: Coincident(g4,g5)
    c: Vertical(g5)
    c: Coincident(g5,g6)
    c: Horizontal(g6)
    c: Distance(g-6,g5) = 3
    c: Distance(g4,g-3) = 3
    c: Parallel(g4,g-3)
    c: Distance(g-4,g3) = 6
    c: Distance(g-5,g2) = 6
    c: PointOnObject(g1,g-4)
    c: Distance(g0,g-7) = 3
    c: Coincident(g0,g7)
    c: Coincident(g7,g8)
    c: Horizontal(g8)
    c: Coincident(g8,g9)
    c: Coincident(g9,g6)
    c: Vertical(g9)
    c: Distance(g8,g8) = 6
    c: Distance(g8,g0) = 6
    c: Angle(g7,g9) = 0.523599
    c: Distance(g7,g1) = 30
FEATURE [PartDesign::Pocket] Pocket002
  BaseFeature = -> Pocket001
  Direction = (1,0,2e-16)
  Length = 0
  Length2 = 5
  Offset = -7
  Placement = pos=(0,0,0) rot=(1,0,0;1.5708rad)
  Profile = -> Sketch005
  ReferenceAxis = -> Sketch005 [N_Axis]
  Refine = true
  Suppressed = false
  Type = 3
  UpToFace = -> Pocket001 [Face5]
FEATURE [Sketcher::SketchObject] Sketch006
  ArcFitTolerance = 1e-06
  AttachmentSupport = -> [Pocket002]
  ExternalGeometry = -> [Pocket002]
  FullyConstrained = true
  MakeInternals = false
  MapMode = 5
  Placement = pos=(0,-12,2.6e-15) rot=(1,0,0;1.5708rad)
  sketch-geometry (4):
    g0: LineSegment StartX=1.5 StartY=40 StartZ=0 EndX=1.5 EndY=34 EndZ=0
    g1: LineSegment StartX=1.5 StartY=34 StartZ=0 EndX=4.5 EndY=34 EndZ=0
    g2: LineSegment StartX=4.5 StartY=34 StartZ=0 EndX=4.5 EndY=40 EndZ=0
    g3: LineSegment StartX=4.5 StartY=40 StartZ=0 EndX=1.5 EndY=40 EndZ=0
  constraints (12):
    c: Coincident(g0,g1)
    c: Coincident(g1,g2)
    c: Coincident(g2,g3)
    c: Coincident(g3,g0)
    c: Vertical(g0)
    c: Vertical(g2)
    c: Horizontal(g1)
    c: Horizontal(g3)
    c: Distance(g0,g-2) = 1.5
    c: Distance(g2,g0) = 3
    c: PointOnObject(g2,g-3)
    c: PointOnObject(g1,g-4)
FEATURE [PartDesign::Pad] Pad002
  BaseFeature = -> Pocket002
  Direction = (0,-1,2e-16)
  Length = 10
  Length2 = 10
  Placement = pos=(0,0,0) rot=(1,0,0;1.5708rad)
  Profile = -> Sketch006
  ReferenceAxis = -> Sketch006 [N_Axis]
  Refine = true
  Suppressed = false
  Type = 2
FEATURE [PartDesign::LinearPattern] LinearPattern
  BaseFeature = -> Pad002
  Direction = -> Sketch006 [H_Axis]
  Length = 36
  Mode = 1
  Occurrences = 7
  Offset = 6
  Originals = -> [Pad002]
  Placement = pos=(0,0,0) rot=(1,0,0;1.5708rad)
  Refine = true
  Suppressed = false
  TransformMode = 0
FEATURE [Sketcher::SketchObject] Sketch007
  ArcFitTolerance = 1e-06
  AttachmentSupport = -> [LinearPattern]
  ExternalGeometry = -> [LinearPattern]
  FullyConstrained = true
  MakeInternals = false
  MapMode = 5
  Placement = pos=(0,-10,0) rot=(1,0,0;1.5708rad)
  sketch-geometry (2):
    g0: Circle CenterX=63.5 CenterY=62.5 CenterZ=0 NormalX=0 NormalY=0 NormalZ=1 AngleXU=0 Radius=3.25
    g1: Circle CenterX=66.5 CenterY=-53.5 CenterZ=0 NormalX=0 NormalY=0 NormalZ=1 AngleXU=0 Radius=3.25
  constraints (4):
    c: Coincident(g0,g-4)
    c: Coincident(g1,g-3)
    c: Diameter(g1) = 6.5
    c: Diameter(g0) = 6.5
FEATURE [PartDesign::Pocket] Pocket003
  BaseFeature = -> LinearPattern
  Direction = (0,1,-2e-16)
  Length = 5
  Length2 = 5
  Placement = pos=(0,0,0) rot=(1,0,0;1.5708rad)
  Profile = -> Sketch007
  ReferenceAxis = -> Sketch007 [N_Axis]
  Refine = true
  Suppressed = false
  Type = 1
FEATURE [Sketcher::SketchObject] Sketch008
  ArcFitTolerance = 1e-06
  AttachmentSupport = -> [Pocket003]
  ExternalGeometry = -> [Pocket003]
  FullyConstrained = true
  MakeInternals = false
  MapMode = 5
  Placement = pos=(0,-3e-16,0) rot=(-1,0,0;1.5708rad)
  sketch-geometry (2):
    g0: Circle CenterX=63.5 CenterY=-62.5 CenterZ=0 NormalX=0 NormalY=0 NormalZ=1 AngleXU=0 Radius=4.5
    g1: Circle CenterX=66.5 CenterY=53.5 CenterZ=0 NormalX=0 NormalY=0 NormalZ=1 AngleXU=0 Radius=4.5
  constraints (4):
    c: Coincident(g0,g-4)
    c: Coincident(g1,g-3)
    c: Diameter(g1) = 9
    c: Diameter(g0) = 9
FEATURE [PartDesign::Pocket] Pocket004
  BaseFeature = -> Pocket003
  Direction = (0,-1,-2e-16)
  Length = 5
  Length2 = 5
  Placement = pos=(0,0,0) rot=(1,0,0;1.5708rad)
  Profile = -> Sketch008
  ReferenceAxis = -> Sketch008 [N_Axis]
  Refine = true
  Suppressed = false
  Type = 0
FEATURE [Sketcher::SketchObject] Sketch009
  ArcFitTolerance = 1e-06
  AttachmentSupport = -> [Pocket004]
  ExternalGeometry = -> [Pocket004]
  FullyConstrained = true
  MakeInternals = false
  MapMode = 5
  Placement = pos=(0,-3e-16,0) rot=(-1,0,0;1.5708rad)
  sketch-geometry (3):
    g0: Circle CenterX=50 CenterY=51 CenterZ=0 NormalX=0 NormalY=0 NormalZ=1 AngleXU=0 Radius=3
    g1: Circle CenterX=50 CenterY=-16 CenterZ=0 NormalX=0 NormalY=0 NormalZ=1 AngleXU=0 Radius=3
    g2: LineSegment [constr] StartX=50 StartY=51 StartZ=0 EndX=50 EndY=-16 EndZ=0
  constraints (8):
    c: Diameter(g1) = 6
    c: Diameter(g0) = 6
    c: Distance(g0,g-2) = 50
    c: Coincident(g2,g0)
    c: Coincident(g2,g1)
    c: Vertical(g2)
    c: DistanceY(g2,g2) = 67
    c: Distance(g0,g-3) = 19
FEATURE [PartDesign::Pocket] Pocket005
  BaseFeature = -> Pocket004
  Direction = (0,-1,-2e-16)
  Length = 5
  Length2 = 5
  Placement = pos=(0,0,0) rot=(1,0,0;1.5708rad)
  Profile = -> Sketch009
  ReferenceAxis = -> Sketch009 [N_Axis]
  Refine = true
  Suppressed = false
  Type = 1
FEATURE [Sketcher::SketchObject] Sketch010
  ArcFitTolerance = 1e-06
  AttachmentSupport = -> [Pocket005]
  ExternalGeometry = -> [Pocket005]
  FullyConstrained = true
  MakeInternals = false
  MapMode = 5
  Placement = pos=(0,-10,0) rot=(1,0,0;1.5708rad)
  sketch-geometry (2):
    g0: Circle CenterX=50 CenterY=16 CenterZ=0 NormalX=0 NormalY=0 NormalZ=1 AngleXU=0 Radius=6
    g1: Circle CenterX=50 CenterY=-51 CenterZ=0 NormalX=0 NormalY=0 NormalZ=1 AngleXU=0 Radius=6
  constraints (4):
    c: Coincident(g0,g-4)
    c: Coincident(g1,g-3)
    c: Diameter(g1) = 12
    c: Diameter(g0) = 12
FEATURE [PartDesign::Pocket] Pocket006
  BaseFeature = -> Pocket005
  Direction = (0,1,-2e-16)
  Length = 5.5
  Length2 = 30
  Midplane = true
  Placement = pos=(0,0,0) rot=(1,0,0;1.5708rad)
  Profile = -> Sketch010
  ReferenceAxis = -> Sketch010 [N_Axis]
  Refine = true
  Suppressed = false
  Type = 4
FEATURE [PartDesign::Fillet] Fillet001
  Base = -> Pocket006 [Edge24,Edge25,Edge28,Edge32,Edge35,Edge40]
  BaseFeature = -> Pocket006
  Placement = pos=(0,0,0) rot=(1,0,0;1.5708rad)
  Radius = 3
  Refine = true
  SupportTransform = false
  Suppressed = false
  UseAllEdges = false
FEATURE [PartDesign::Fillet] Fillet002
  Base = -> Fillet001 [Edge113]
  BaseFeature = -> Fillet001
  Placement = pos=(0,0,0) rot=(1,0,0;1.5708rad)
  Radius = 0.5
  Refine = true
  SupportTransform = false
  Suppressed = false
  UseAllEdges = false
FEATURE [PartDesign::Fillet] Fillet003
  Base = -> Fillet002 [Edge76,Edge50]
  BaseFeature = -> Fillet002
  Placement = pos=(0,0,0) rot=(1,0,0;1.5708rad)
  Radius = 1
  Refine = true
  SupportTransform = false
  Suppressed = false
  UseAllEdges = false
FEATURE [PartDesign::Fillet] Fillet004
  Base = -> Fillet003 [Edge63,Edge65]
  BaseFeature = -> Fillet003
  Placement = pos=(0,0,0) rot=(1,0,0;1.5708rad)
  Radius = 3
  Refine = true
  SupportTransform = false
  Suppressed = false
  UseAllEdges = false
FEATURE [PartDesign::Fillet] Fillet005
  Base = -> Fillet004 [Edge36]
  BaseFeature = -> Fillet004
  Placement = pos=(0,0,0) rot=(1,0,0;1.5708rad)
  Radius = 3
  Refine = true
  SupportTransform = false
  Suppressed = false
  UseAllEdges = false
FEATURE [Sketcher::SketchObject] Sketch014
  ArcFitTolerance = 1e-06
  AttachmentSupport = -> [Pocket004]
  ExternalGeometry = -> [Pocket004]
  FullyConstrained = true
  MakeInternals = false
  MapMode = 5
  Placement = pos=(0,-10,0) rot=(1,0,0;1.5708rad)
  sketch-geometry (2):
    g0: Circle CenterX=63.5 CenterY=62.5 CenterZ=0 NormalX=0 NormalY=0 NormalZ=1 AngleXU=0 Radius=5.5
    g1: Circle CenterX=66.5 CenterY=-53.5 CenterZ=0 NormalX=0 NormalY=0 NormalZ=1 AngleXU=0 Radius=5.5
  constraints (4):
    c: Coincident(g0,g-3)
    c: Coincident(g1,g-4)
    c: Diameter(g1) = 11
    c: Diameter(g0) = 11
FEATURE [PartDesign::Pocket] Pocket007
  BaseFeature = -> Fillet005
  Direction = (0,1,-2e-16)
  Length = 2
  Length2 = 5
  Placement = pos=(0,0,0) rot=(1,0,0;1.5708rad)
  Profile = -> Sketch014
  ReferenceAxis = -> Sketch014 [N_Axis]
  Refine = true
  Suppressed = false
  Type = 0
FEATURE [PartDesign::Mirrored] Mirrored
  BaseFeature = -> Pocket007
  MirrorPlane = -> YZ_Plane001
  Placement = pos=(0,0,0) rot=(1,0,0;1.5708rad)
  Refine = true
  Suppressed = false
  TransformMode = 1
FEATURE [Sketcher::SketchObject] Sketch015
  ArcFitTolerance = 1e-06
  FullyConstrained = true
  MakeInternals = false
  MapMode = 5
  Placement = pos=(0,-19.5589,-3.09782) rot=(-1,0,0;1.41372rad)
  sketch-geometry (1):
    g0: Circle CenterX=0 CenterY=-7.5 CenterZ=0 NormalX=0 NormalY=0 NormalZ=1 AngleXU=0 Radius=39
  constraints (3):
    c: PointOnObject(g0,g-2)
    c: Diameter(g0) = 78
    c: Distance(g0,g-1) = 7.5
FEATURE [PartDesign::Pocket] Pocket012
  BaseFeature = -> Mirrored
  Direction = (0,-0.987688,-0.156434)
  Length = 2
  Length2 = 5
  Midplane = true
  Placement = pos=(0,0,0) rot=(1,0,0;1.5708rad)
  Profile = -> Sketch015
  ReferenceAxis = -> Sketch015 [N_Axis]
  Refine = true
  Suppressed = false
  Type = 1
FEATURE [Sketcher::SketchObject] Sketch016
  ArcFitTolerance = 1e-06
  AttachmentSupport = -> [Pocket012]
  ExternalGeometry = -> [Pocket012]
  FullyConstrained = true
  MakeInternals = false
  MapMode = 5
  Placement = pos=(0,-19.5589,-3.09782) rot=(-1,0,0;1.41372rad)
  sketch-geometry (4):
    g0: ArcOfCircle CenterX=0 CenterY=-7.5 CenterZ=0 NormalX=0 NormalY=0 NormalZ=1 AngleXU=0 Radius=39 StartAngle=3.62672 EndAngle=5.79806
    g1: ArcOfCircle CenterX=0 CenterY=-7.5 CenterZ=0 NormalX=0 NormalY=0 NormalZ=1 AngleXU=0 Radius=51 StartAngle=3.96943 EndAngle=5.45535
    g2: LineSegment StartX=-34.5 StartY=-45.06 StartZ=0 EndX=-34.5 EndY=-25.6865 EndZ=0
    g3: LineSegment StartX=34.5 StartY=-25.6865 StartZ=0 EndX=34.5 EndY=-45.06 EndZ=0
  constraints (12):
    c: Coincident(g2,g1)
    c: Coincident(g2,g0)
    c: Coincident(g3,g0)
    c: Coincident(g3,g1)
    c: Vertical(g2)
    c: Coincident(g0,g-5)
    c: Radius(g0) = 39
    c: Distance(g1,g0) = 12
    c: Coincident(g1,g0)
    c: Vertical(g3)
    c: PointOnObject(g-8,g3)
    c: PointOnObject(g-9,g2)
FEATURE [PartDesign::Pad] Pad003
  BaseFeature = -> Pocket012
  Direction = (0,0.987688,0.156434)
  Length = 10
  Length2 = 10
  Placement = pos=(0,0,0) rot=(1,0,0;1.5708rad)
  Profile = -> Sketch016
  ReferenceAxis = -> Sketch016 [N_Axis]
  Refine = true
  Suppressed = false
  Type = 3
  UpToFace = -> Pocket012 [Face28]
FEATURE [Sketcher::SketchObject] Sketch017
  ArcFitTolerance = 1e-06
  AttachmentSupport = -> [Pad003]
  ExternalGeometry = -> [Pad003]
  FullyConstrained = true
  MakeInternals = false
  MapMode = 5
  Placement = pos=(0,-19.5589,-3.09782) rot=(-1,0,0;1.41372rad)
  sketch-geometry (4):
    g0: LineSegment StartX=34.5 StartY=0 StartZ=0 EndX=34.5 EndY=-67.3488 EndZ=0
    g1: LineSegment StartX=34.5 StartY=-67.3488 StartZ=0 EndX=37.5 EndY=-67.3488 EndZ=0
    g2: LineSegment StartX=37.5 StartY=-67.3488 StartZ=0 EndX=37.5 EndY=0 EndZ=0
    g3: LineSegment StartX=37.5 StartY=0 StartZ=0 EndX=34.5 EndY=0 EndZ=0
  constraints (12):
    c: Coincident(g0,g1)
    c: Coincident(g1,g2)
    c: Coincident(g2,g3)
    c: Coincident(g3,g0)
    c: Vertical(g0)
    c: Vertical(g2)
    c: Horizontal(g1)
    c: Horizontal(g3)
    c: PointOnObject(g-1,g3)
    c: PointOnObject(g1,g-3)
    c: PointOnObject(g-5,g2)
    c: PointOnObject(g-4,g0)
FEATURE [PartDesign::Pocket] Pocket013
  BaseFeature = -> Pad003
  Direction = (0,-0.987688,-0.156434)
  Length = 0
  Length2 = 5
  Placement = pos=(0,0,0) rot=(1,0,0;1.5708rad)
  Profile = -> Sketch017
  ReferenceAxis = -> Sketch017 [N_Axis]
  Refine = true
  Suppressed = false
  Type = 3
  UpToFace = -> Pad003 [Face84]
FEATURE [PartDesign::LinearPattern] LinearPattern001
  BaseFeature = -> Pocket013
  Direction = -> X_Axis001
  Length = 66
  Mode = 1
  Occurrences = 12
  Offset = 6
  Originals = -> [Pocket013]
  Placement = pos=(0,0,0) rot=(1,0,0;1.5708rad)
  Refine = true
  Reversed = true
  Suppressed = false
  TransformMode = 0
FEATURE [Sketcher::SketchObject] Sketch019
  ArcFitTolerance = 1e-06
  AttachmentSupport = -> [LinearPattern001]
  ExternalGeometry = -> [LinearPattern001]
  FullyConstrained = true
  MakeInternals = false
  MapMode = 5
  Placement = pos=(0,-22.5219,-3.56712) rot=(1,0,0;1.72788rad)
  sketch-geometry (16):
    g0: Circle CenterX=0 CenterY=7.5 CenterZ=0 NormalX=0 NormalY=0 NormalZ=1 AngleXU=0 Radius=41
    g1: ArcOfCircle CenterX=0 CenterY=7.5 CenterZ=0 NormalX=0 NormalY=0 NormalZ=1 AngleXU=0 Radius=44 StartAngle=4.3176 EndAngle=5.10718
    g2: ArcOfCircle CenterX=22 CenterY=-55.0913 CenterZ=0 NormalX=0 NormalY=0 NormalZ=1 AngleXU=0 Radius=18 StartAngle=2.17527 EndAngle=2.9376
    g3: ArcOfCircle CenterX=-22 CenterY=-55.0913 CenterZ=0 NormalX=0 NormalY=0 NormalZ=1 AngleXU=0 Radius=18 StartAngle=0.20399 EndAngle=0.966323
    g4: LineSegment StartX=-4.37321 StartY=-51.4449 StartZ=0 EndX=-2.66496 EndY=-59.7026 EndZ=0
    g5: LineSegment StartX=-1.68569 StartY=-60.5 StartZ=0 EndX=1.68569 EndY=-60.5 EndZ=0
    g6: LineSegment StartX=2.66496 StartY=-59.7026 StartZ=0 EndX=4.37321 EndY=-51.4449 EndZ=0
    g7: LineSegment [constr] StartX=0 StartY=-60.5 StartZ=0 EndX=0 EndY=-36.5 EndZ=0
    g8: ArcOfCircle CenterX=1.68569 CenterY=-59.5 CenterZ=0 NormalX=0 NormalY=0 NormalZ=1 AngleXU=0 Radius=1 StartAngle=4.71239 EndAngle=6.0792
    g9: GeomPoint [constr] X=2.5 Y=-60.5 Z=0
    g10: ArcOfCircle CenterX=-1.68569 CenterY=-59.5 CenterZ=0 NormalX=0 NormalY=0 NormalZ=1 AngleXU=0 Radius=1 StartAngle=3.34558 EndAngle=4.71239
    g11: GeomPoint [constr] X=-2.5 Y=-60.5 Z=0
    g12: LineSegment StartX=11.7701 StartY=-40.2808 StartZ=0 EndX=18.3525 EndY=-35.7342 EndZ=0
    g13: ArcOfCircle CenterX=17.5 CenterY=-34.5 CenterZ=0 NormalX=0 NormalY=0 NormalZ=1 AngleXU=0 Radius=1.5 StartAngle=5.31686 EndAngle=8.24877
    g14: LineSegment StartX=-11.7701 StartY=-40.2808 StartZ=0 EndX=-18.3525 EndY=-35.7342 EndZ=0
    g15: ArcOfCircle CenterX=-17.5 CenterY=-34.5 CenterZ=0 NormalX=0 NormalY=0 NormalZ=1 AngleXU=0 Radius=1.5 StartAngle=1.17601 EndAngle=4.10792
  constraints (39):
    c: Diameter(g0) = 82
    c: Tangent(g3,g4) = 1.5708
    c: Horizontal(g5)
    c: Tangent(g6,g2) = 1.5708
    c: Symmetric(g11,g9,g7)
    c: PointOnObject(g7,g1)
    c: Vertical(g7)
    c: Coincident(g1,g0)
    c: Radius(g1) = 44
    c: Distance(g0,g5) = 68
    c: Distance(g11,g9) = 5
    c: Radius(g3) = 18
    c: Radius(g2) = 18
    c: Distance(g3,g7) = 22
    c: Distance(g2,g7) = 22
    c: PointOnObject(g9,g5)
    c: PointOnObject(g9,g6)
    c: Tangent(g5,g8) = -1.5708
    c: Tangent(g6,g8) = -1.5708
    c: PointOnObject(g11,g4)
    c: PointOnObject(g11,g5)
    c: Tangent(g4,g10) = -1.5708
    c: Tangent(g5,g10) = -1.5708
    c: Radius(g10) = 1
    c: Radius(g8) = 1
    c: Tangent(g13,g1) = 1.5708
    c: Tangent(g13,g12) = -1.5708
    c: Tangent(g12,g2) = 1.5708
    c: Radius(g13) = 1.5
    c: Distance(g12,g12) = 8
    c: Distance(g13,g7) = 17.5
    c: Tangent(g14,g3) = -1.5708
    c: Tangent(g15,g1) = 1.5708
    c: Tangent(g15,g14) = 1.5708
    c: Radius(g15) = 1.5
    c: Distance(g14,g14) = 8
    c: Distance(g15,g7) = 17.5
    c: Coincident(g0,g-3)
    c: PointOnObject(g7,g-2)
FEATURE [PartDesign::Pocket] Pocket014
  BaseFeature = -> LinearPattern001
  Direction = (0,0.987688,0.156434)
  Length = 1
  Length2 = 5
  Placement = pos=(0,0,0) rot=(1,0,0;1.5708rad)
  Profile = -> Sketch019
  ReferenceAxis = -> Sketch019 [N_Axis]
  Refine = true
  Suppressed = false
  Type = 0
FEATURE [Sketcher::SketchObject] Sketch020
  ArcFitTolerance = 1e-06
  AttachmentSupport = -> [Pocket014]
  ExternalGeometry = -> [Pocket014]
  FullyConstrained = true
  MakeInternals = false
  MapMode = 5
  Placement = pos=(-3e-15,-19.5589,-3.09782) rot=(-1,0,0;1.41372rad)
  sketch-geometry (8):
    g0: ArcOfCircle CenterX=2.7e-15 CenterY=-7.5 CenterZ=0 NormalX=0 NormalY=0 NormalZ=1 AngleXU=0 Radius=39 StartAngle=5.41052 EndAngle=10.2974
    g1: ArcOfCircle CenterX=2.7e-15 CenterY=-7.5 CenterZ=0 NormalX=0 NormalY=0 NormalZ=1 AngleXU=0 Radius=48 StartAngle=5.41052 EndAngle=5.82269
    g2: LineSegment StartX=-30.8538 StartY=-44.2701 StartZ=0 EndX=-25.0687 EndY=-37.3757 EndZ=0
    g3: LineSegment StartX=30.8538 StartY=-44.2701 StartZ=0 EndX=25.0687 EndY=-37.3757 EndZ=0
    g4: LineSegment StartX=-43 StartY=-28.8307 StartZ=0 EndX=-43 EndY=13.8307 EndZ=0
    g5: LineSegment StartX=43 StartY=13.8307 StartZ=0 EndX=43 EndY=-28.8307 EndZ=0
    g6: ArcOfCircle CenterX=2.7e-15 CenterY=-7.5 CenterZ=0 NormalX=0 NormalY=0 NormalZ=1 AngleXU=0 Radius=48 StartAngle=3.60209 EndAngle=4.01426
    g7: ArcOfCircle CenterX=2.7e-15 CenterY=-7.5 CenterZ=0 NormalX=0 NormalY=0 NormalZ=1 AngleXU=0 Radius=48 StartAngle=0.460493 EndAngle=2.6811
  constraints (24):
    c: Coincident(g0,g-3)
    c: Coincident(g1,g0)
    c: Coincident(g2,g6)
    c: Coincident(g2,g0)
    c: Coincident(g3,g1)
    c: Coincident(g3,g0)
    c: Distance(g0,g1) = 9
    c: PointOnObject(g4,g6)
    c: Vertical(g4)
    c: Vertical(g5)
    c: PointOnObject(g4,g-7)
    c: PointOnObject(g5,g-6)
    c: Equal(g1,g6)
    c: Coincident(g1,g6)
    c: Coincident(g1,g5)
    c: Coincident(g6,g4)
    c: Coincident(g7,g4)
    c: Coincident(g7,g5)
    c: Coincident(g7,g0)
    c: PointOnObject(g0,g-3)
    c: PointOnObject(g0,g2)
    c: PointOnObject(g0,g3)
    c: Angle(g2,g3) = 1.39626
    c: Angle(g2,g-2) = 0.698132
FEATURE [PartDesign::Pad] Pad004
  BaseFeature = -> Pocket014
  Direction = (0,0.987688,0.156434)
  Length = 5
  Length2 = 10
  Placement = pos=(0,0,0) rot=(1,0,0;1.5708rad)
  Profile = -> Sketch020
  ReferenceAxis = -> Sketch020 [N_Axis]
  Refine = true
  Suppressed = false
  Type = 0
FEATURE [Sketcher::SketchObject] Sketch028
  ArcFitTolerance = 1e-06
  AttachmentSupport = -> [Pad004]
  ExternalGeometry = -> [Pad004]
  FullyConstrained = true
  MakeInternals = false
  MapMode = 5
  Placement = pos=(0,-14.6204,-2.31565) rot=(-1,0,0;1.41372rad)
  sketch-geometry (5):
    g0: ArcOfCircle CenterX=2e-16 CenterY=-7.5 CenterZ=0 NormalX=0 NormalY=0 NormalZ=1 AngleXU=0 Radius=39 StartAngle=0.449314 EndAngle=0.667697
    g1: LineSegment StartX=30.6247 StartY=16.648 StartZ=0 EndX=32.5178 EndY=17.8309 EndZ=0
    g2: ArcOfCircle CenterX=34.77 CenterY=14.2267 CenterZ=0 NormalX=0 NormalY=0 NormalZ=1 AngleXU=0 Radius=4.25 StartAngle=5.27089 EndAngle=8.41249
    g3: LineSegment StartX=37.0221 StartY=10.6225 StartZ=0 EndX=35.1291 EndY=9.43957 EndZ=0
    g4: LineSegment [constr] StartX=34.77 StartY=14.2267 StartZ=0 EndX=33.0739 EndY=13.1669 EndZ=0
  constraints (14):
    c: Coincident(g0,g1)
    c: Tangent(g1,g2) = 1.5708
    c: Tangent(g2,g3) = 1.5708
    c: Coincident(g4,g2)
    c: PointOnObject(g4,g0)
    c: Coincident(g0,g3)
    c: PointOnObject(g0,g4)
    c: Distance(g4,g4) = 2
    c: Parallel(g4,g1)
    c: Parallel(g3,g1)
    c: Radius(g2) = 4.25
    c: Angle(g-1,g4) = 0.558505
    c: PointOnObject(g4,g-3)
    c: Coincident(g0,g-3)
FEATURE [PartDesign::Pocket] Pocket015
  BaseFeature = -> Pad004
  Direction = (0,-0.987688,-0.156434)
  Length = 2.5
  Length2 = 5
  Placement = pos=(0,0,0) rot=(1,0,0;1.5708rad)
  Profile = -> Sketch028
  ReferenceAxis = -> Sketch028 [N_Axis]
  Refine = true
  Suppressed = false
  Type = 0
FEATURE [Sketcher::SketchObject] Sketch029
  ArcFitTolerance = 1e-06
  AttachmentSupport = -> [Pocket015]
  ExternalGeometry = -> [Pocket015]
  FullyConstrained = true
  MakeInternals = false
  MapMode = 5
  Placement = pos=(0,-17.0896,-2.70673) rot=(-1,0,0;1.41372rad)
  sketch-geometry (8):
    g0: ArcOfCircle CenterX=0 CenterY=-7.5 CenterZ=0 NormalX=0 NormalY=0 NormalZ=1 AngleXU=0 Radius=39 StartAngle=0.239875 EndAngle=0.667697
    g1: LineSegment StartX=30.6247 StartY=16.648 StartZ=0 EndX=32.5178 EndY=17.8309 EndZ=0
    g2: LineSegment StartX=37.8833 StartY=1.76565 StartZ=0 EndX=39.981 EndY=2.52913 EndZ=0
    g3: ArcOfCircle CenterX=38.5274 CenterY=6.52283 CenterZ=0 NormalX=0 NormalY=0 NormalZ=1 AngleXU=0 Radius=4.25 StartAngle=5.06145 EndAngle=6.63225
    g4: ArcOfCircle CenterX=0 CenterY=-7.5 CenterZ=0 NormalX=0 NormalY=0 NormalZ=1 AngleXU=0 Radius=45.25 StartAngle=0.349066 EndAngle=0.558505
    g5: ArcOfCircle CenterX=34.77 CenterY=14.2267 CenterZ=0 NormalX=0 NormalY=0 NormalZ=1 AngleXU=0 Radius=4.25 StartAngle=0.558505 EndAngle=2.1293
    g6: LineSegment [constr] StartX=38.3742 StartY=16.4788 StartZ=0 EndX=34.77 EndY=14.2267 EndZ=0
    g7: LineSegment [constr] StartX=42.5211 StartY=7.97641 StartZ=0 EndX=38.5274 EndY=6.52283 EndZ=0
  constraints (18):
    c: Coincident(g1,g0)
    c: Coincident(g2,g0)
    c: Tangent(g5,g1) = 1.5708
    c: Tangent(g3,g2) = -1.5708
    c: Tangent(g4,g3) = -1.5708
    c: Tangent(g5,g4) = -1.5708
    c: Coincident(g0,g-5)
    c: Coincident(g5,g-4)
    c: Coincident(g0,g-3)
    c: Coincident(g4,g0)
    c: PointOnObject(g4,g-4)
    c: Coincident(g6,g4)
    c: Coincident(g6,g5)
    c: Coincident(g7,g3)
    c: Coincident(g7,g3)
    c: Radius(g3) = 4.25
    c: Parallel(g2,g7)
    c: Angle(g7,g6) = 0.20944
FEATURE [PartDesign::Pocket] Pocket016
  BaseFeature = -> Pocket015
  Direction = (0,-0.987688,-0.156434)
  Length = 0
  Length2 = 5
  Placement = pos=(0,0,0) rot=(1,0,0;1.5708rad)
  Profile = -> Sketch029
  ReferenceAxis = -> Sketch029 [N_Axis]
  Refine = true
  Suppressed = false
  Type = 3
  UpToFace = -> Pocket015 [Face57]
FEATURE [PartDesign::Point] DatumPoint
  AttacherType = Attacher::AttachEnginePoint
  AttachmentSupport = -> [Pocket016]
  MapMode = 36
  Placement = pos=(-2.7e-15,-15.7937,5.09201) rot=(0.220642,0.972348,0.076525;0.685251rad)
FEATURE [PartDesign::Point] DatumPoint001
  AttacherType = Attacher::AttachEnginePoint
  AttachmentSupport = -> [Pocket016]
  MapMode = 36
  Placement = pos=(-1.42e-14,-22.7075,3.99697) rot=(1,0,0;0.15708rad)
FEATURE [PartDesign::Line] DatumLine
  AttacherType = Attacher::AttachEngineLine
  AttachmentSupport = -> [DatumPoint,DatumPoint001]
  Length = 20
  MapMode = 29
  Placement = pos=(-2.7e-15,-15.7937,5.09201) rot=(1,0,0;1.72788rad)
  ResizeMode = 0
FEATURE [PartDesign::PolarPattern] PolarPattern
  Angle = 360
  Axis = -> DatumLine
  BaseFeature = -> Pocket016
  Mode = 1
  Occurrences = 2
  Offset = 120
  Originals = -> [Pocket015,Pocket016]
  Placement = pos=(0,0,0) rot=(1,0,0;1.5708rad)
  Refine = true
  Reversed = true
  Suppressed = false
  TransformMode = 0
FEATURE [PartDesign::PolarPattern] PolarPattern001
  Angle = 360
  Axis = -> DatumLine
  BaseFeature = -> PolarPattern
  Mode = 1
  Occurrences = 2
  Offset = 180
  Originals = -> [Pocket015,Pocket016]
  Placement = pos=(0,0,0) rot=(1,0,0;1.5708rad)
  Refine = true
  Reversed = true
  Suppressed = false
  TransformMode = 0
FEATURE [PartDesign::PolarPattern] PolarPattern002
  Angle = 360
  Axis = -> DatumLine
  BaseFeature = -> PolarPattern001
  Mode = 1
  Occurrences = 2
  Offset = 60
  Originals = -> [Pocket015,Pocket016]
  Placement = pos=(0,0,0) rot=(1,0,0;1.5708rad)
  Refine = true
  Suppressed = false
  TransformMode = 0
FEATURE [Sketcher::SketchObject] Sketch030
  ArcFitTolerance = 1e-06
  AttachmentSupport = -> [PolarPattern002]
  ExternalGeometry = -> [PolarPattern002]
  FullyConstrained = true
  MakeInternals = false
  MapMode = 5
  Placement = pos=(0,-14.6204,-2.31565) rot=(-1,0,0;1.41372rad)
  sketch-geometry (10):
    g0: Circle [constr] CenterX=0 CenterY=-7.5 CenterZ=0 NormalX=0 NormalY=0 NormalZ=1 AngleXU=0 Radius=42.25
    g1: LineSegment [constr] StartX=34.77 StartY=14.2267 StartZ=0 EndX=0 EndY=-7.5 EndZ=0
    g2: Circle CenterX=39.702 CenterY=6.95035 CenterZ=0 NormalX=0 NormalY=0 NormalZ=1 AngleXU=0 Radius=1.25
    g3: Circle CenterX=32.3654 CenterY=-34.6578 CenterZ=0 NormalX=0 NormalY=0 NormalZ=1 AngleXU=0 Radius=1.25
    g4: Circle CenterX=-39.702 CenterY=-21.9504 CenterZ=0 NormalX=0 NormalY=0 NormalZ=1 AngleXU=0 Radius=1.25
    g5: Circle CenterX=-32.3654 CenterY=19.6578 CenterZ=0 NormalX=0 NormalY=0 NormalZ=1 AngleXU=0 Radius=1.25
    g6: LineSegment [constr] StartX=0 StartY=-7.5 StartZ=0 EndX=39.702 EndY=6.95035 EndZ=0
    g7: LineSegment [constr] StartX=0 StartY=-7.5 StartZ=0 EndX=32.3654 EndY=-34.6578 EndZ=0
    g8: LineSegment [constr] StartX=-39.702 StartY=-21.9504 StartZ=0 EndX=0 EndY=-7.5 EndZ=0
    g9: LineSegment [constr] StartX=-32.3654 StartY=19.6578 StartZ=0 EndX=0 EndY=-7.5 EndZ=0
  constraints (24):
    c: Coincident(g0,g-3)
    c: Distance(g-4,g0) = 1.25
    c: Coincident(g1,g-4)
    c: Coincident(g1,g0)
    c: PointOnObject(g2,g0)
    c: PointOnObject(g3,g0)
    c: PointOnObject(g4,g0)
    c: PointOnObject(g5,g0)
    c: Coincident(g6,g0)
    c: Coincident(g6,g2)
    c: Coincident(g7,g0)
    c: Coincident(g7,g3)
    c: Coincident(g8,g4)
    c: Coincident(g8,g0)
    c: Coincident(g9,g5)
    c: Coincident(g9,g0)
    c: Diameter(g5) = 2.5
    c: Diameter(g4) = 2.5
    c: Diameter(g2) = 2.5
    c: Diameter(g3) = 2.5
    c: Angle(g6,g1) = 0.20944
    c: Angle(g7,g6) = 1.0472
    c: Angle(g9,g8) = 1.0472
    c: Angle(g8,g6) = 3.14159
FEATURE [PartDesign::Pocket] Pocket017
  BaseFeature = -> PolarPattern002
  Direction = (0,-0.987688,-0.156434)
  Length = 3
  Length2 = 5
  Placement = pos=(0,0,0) rot=(1,0,0;1.5708rad)
  Profile = -> Sketch030
  ReferenceAxis = -> Sketch030 [N_Axis]
  Refine = true
  Suppressed = false
  Type = 0
FEATURE [Sketcher::SketchObject] Sketch031
  ArcFitTolerance = 1e-06
  AttachmentSupport = -> [Pocket017]
  ExternalGeometry = -> [Pocket017]
  FullyConstrained = true
  MakeInternals = false
  MapMode = 5
  Placement = pos=(0,-21.5342,-3.41069) rot=(1,0,0;1.72788rad)
  sketch-geometry (1):
    g0: Circle CenterX=0 CenterY=-45.5 CenterZ=0 NormalX=0 NormalY=0 NormalZ=1 AngleXU=0 Radius=4.5
  constraints (3):
    c: PointOnObject(g0,g-2)
    c: Diameter(g0) = 9
    c: Distance(g0,g-3) = 15
FEATURE [PartDesign::Pad] Pad005
  BaseFeature = -> Pocket017
  Direction = (0,-0.987688,-0.156434)
  Length = 10
  Length2 = 10
  Placement = pos=(0,0,0) rot=(1,0,0;1.5708rad)
  Profile = -> Sketch031
  ReferenceAxis = -> Sketch031 [N_Axis]
  Refine = true
  Reversed = true
  Suppressed = false
  Type = 0
FEATURE [Sketcher::SketchObject] Sketch032
  ArcFitTolerance = 1e-06
  AttachmentSupport = -> [Pad005]
  ExternalGeometry = -> [Pad005]
  FullyConstrained = true
  MakeInternals = false
  MapMode = 5
  Placement = pos=(0,-11.6574,-1.84634) rot=(-1,0,0;1.41372rad)
  sketch-geometry (1):
    g0: Circle CenterX=0 CenterY=45.5 CenterZ=0 NormalX=0 NormalY=0 NormalZ=1 AngleXU=0 Radius=3
  constraints (2):
    c: Coincident(g0,g-3)
    c: Diameter(g0) = 6
FEATURE [PartDesign::Pocket] Pocket018
  BaseFeature = -> Pad005
  Direction = (0,-0.987688,-0.156434)
  Length = 5
  Length2 = 5
  Placement = pos=(0,0,0) rot=(1,0,0;1.5708rad)
  Profile = -> Sketch032
  ReferenceAxis = -> Sketch032 [N_Axis]
  Refine = true
  Suppressed = false
  Type = 1
FEATURE [Sketcher::SketchObject] Sketch033
  ArcFitTolerance = 1e-06
  AttachmentSupport = -> [Pocket018]
  ExternalGeometry = -> [Pocket018]
  FullyConstrained = true
  MakeInternals = false
  MapMode = 5
  Placement = pos=(0,-14.6204,-2.31565) rot=(-1,0,0;1.41372rad)
  sketch-geometry (4):
    g0: ArcOfCircle CenterX=0 CenterY=-7.5 CenterZ=0 NormalX=0 NormalY=0 NormalZ=1 AngleXU=0 Radius=39 StartAngle=0.872665 EndAngle=2.26893
    g1: ArcOfCircle CenterX=0 CenterY=-7.5 CenterZ=0 NormalX=0 NormalY=0 NormalZ=1 AngleXU=0 Radius=48 StartAngle=0.872665 EndAngle=2.26893
    g2: LineSegment StartX=-30.8538 StartY=29.2701 StartZ=0 EndX=-25.0687 EndY=22.3757 EndZ=0
    g3: LineSegment StartX=25.0687 StartY=22.3757 StartZ=0 EndX=30.8538 EndY=29.2701 EndZ=0
  constraints (12):
    c: Coincident(g2,g1)
    c: Coincident(g2,g0)
    c: Coincident(g3,g0)
    c: Coincident(g3,g1)
    c: PointOnObject(g1,g-3)
    c: PointOnObject(g0,g-4)
    c: Coincident(g0,g-4)
    c: Coincident(g1,g0)
    c: PointOnObject(g0,g2)
    c: PointOnObject(g0,g3)
    c: Angle(g3,g2) = 1.39626
    c: Angle(g-2,g2) = 0.698132
FEATURE [PartDesign::Pocket] Pocket019
  BaseFeature = -> Pocket018
  Direction = (0,-0.987688,-0.156434)
  Length = 0
  Length2 = 5
  Placement = pos=(0,0,0) rot=(1,0,0;1.5708rad)
  Profile = -> Sketch033
  ReferenceAxis = -> Sketch033 [N_Axis]
  Refine = true
  Suppressed = false
  Type = 3
  UpToFace = -> Pocket018 [Face57]
FEATURE [Sketcher::SketchObject] Sketch034
  ArcFitTolerance = 1e-06
  AttachmentSupport = -> [Pocket019]
  ExternalGeometry = -> [Pocket019]
  FullyConstrained = true
  MakeInternals = false
  MapMode = 5
  Placement = pos=(0,-11.6574,-1.84634) rot=(-1,0,0;1.41372rad)
  sketch-geometry (1):
    g0: Circle CenterX=0 CenterY=45.5 CenterZ=0 NormalX=0 NormalY=0 NormalZ=1 AngleXU=0 Radius=4.5
  constraints (2):
    c: Coincident(g0,g-3)
    c: Equal(g0,g-3)
FEATURE [PartDesign::Pad] Pad006
  BaseFeature = -> Pocket019
  Direction = (0,0.987688,0.156434)
  Length = 1
  Length2 = 10
  Placement = pos=(0,0,0) rot=(1,0,0;1.5708rad)
  Profile = -> Sketch034
  ReferenceAxis = -> Sketch034 [N_Axis]
  Refine = true
  Suppressed = false
  Type = 0
FEATURE [PartDesign::Chamfer] Chamfer
  Angle = 45
  Base = -> Pad006 [Edge692]
  BaseFeature = -> Pad006
  ChamferType = 0
  FlipDirection = false
  Placement = pos=(0,0,0) rot=(1,0,0;1.5708rad)
  Refine = true
  Size = 1.5
  Size2 = 1
  SupportTransform = false
  Suppressed = false
  UseAllEdges = false
FEATURE [Sketcher::SketchObject] Sketch035
  ArcFitTolerance = 1e-06
  AttachmentSupport = -> [Chamfer]
  ExternalGeometry = -> [Chamfer]
  FullyConstrained = true
  MakeInternals = false
  MapMode = 5
  Placement = pos=(0,-11.6574,-1.84634) rot=(1,0,0;1.72788rad)
  sketch-geometry (1):
    g0: Circle CenterX=0 CenterY=-45.5 CenterZ=0 NormalX=0 NormalY=0 NormalZ=1 AngleXU=0 Radius=1.5
  constraints (2):
    c: Coincident(g0,g-3)
    c: Equal(g0,g-3)
FEATURE [PartDesign::Pocket] Pocket020
  BaseFeature = -> Chamfer
  Direction = (0,0.987688,0.156434)
  Length = 5
  Length2 = 5
  Placement = pos=(0,0,0) rot=(1,0,0;1.5708rad)
  Profile = -> Sketch035
  ReferenceAxis = -> Sketch035 [N_Axis]
  Refine = true
  Suppressed = false
  Type = 1
FEATURE [PartDesign::Chamfer] Chamfer001
  Angle = 45
  Base = -> Pocket020 [Edge3]
  BaseFeature = -> Pocket020
  ChamferType = 0
  FlipDirection = false
  Placement = pos=(0,0,0) rot=(1,0,0;1.5708rad)
  Refine = true
  Size = 0.5
  Size2 = 1
  SupportTransform = false
  Suppressed = false
  UseAllEdges = false
FEATURE [PartDesign::Chamfer] Chamfer002
  Angle = 45
  Base = -> Chamfer001 [Edge236]
  BaseFeature = -> Chamfer001
  ChamferType = 0
  FlipDirection = false
  Placement = pos=(0,0,0) rot=(1,0,0;1.5708rad)
  Refine = true
  Size = 0.5
  Size2 = 1
  SupportTransform = false
  Suppressed = false
  UseAllEdges = false
FEATURE [Sketcher::SketchObject] Sketch036
  ArcFitTolerance = 1e-06
  AttachmentSupport = -> [Chamfer001]
  ExternalGeometry = -> [Chamfer001]
  FullyConstrained = true
  MakeInternals = false
  MapMode = 5
  Placement = pos=(0,-14.6204,-2.31565) rot=(-1,0,0;1.41372rad)
  sketch-geometry (3):
    g0: ArcOfCircle CenterX=0 CenterY=-7.5 CenterZ=0 NormalX=0 NormalY=0 NormalZ=1 AngleXU=0 Radius=45 StartAngle=3.66519 EndAngle=5.75959
    g1: LineSegment StartX=-38.9711 StartY=-30 StartZ=0 EndX=0 EndY=-7.5 EndZ=0
    g2: LineSegment StartX=38.9711 StartY=-30 StartZ=0 EndX=0 EndY=-7.5 EndZ=0
  constraints (8):
    c: Coincident(g0,g-3)
    c: Coincident(g1,g0)
    c: Coincident(g1,g0)
    c: Coincident(g2,g0)
    c: Coincident(g2,g0)
    c: Angle(g1,g2) = 2.0944
    c: Angle(g1,g-2) = 1.0472
    c: Distance(g-3,g0) = 6
FEATURE [PartDesign::Pocket] Pocket021
  BaseFeature = -> Chamfer002
  Direction = (0,-0.987688,-0.156434)
  Length = 5
  Length2 = 5
  Placement = pos=(0,0,0) rot=(1,0,0;1.5708rad)
  Profile = -> Sketch036
  ReferenceAxis = -> Sketch036 [N_Axis]
  Refine = true
  Reversed = true
  Suppressed = false
  Type = 1
FEATURE [Sketcher::SketchObject] Sketch037
  ArcFitTolerance = 1e-06
  AttachmentSupport = -> [Pocket021]
  ExternalGeometry = -> [Pocket021]
  FullyConstrained = true
  MakeInternals = false
  MapMode = 5
  Placement = pos=(7.7e-15,-14.6204,-2.31565) rot=(-1,0,0;1.41372rad)
  sketch-geometry (4):
    g0: ArcOfCircle CenterX=-7.3e-15 CenterY=-7.5 CenterZ=0 NormalX=0 NormalY=0 NormalZ=1 AngleXU=0 Radius=39 StartAngle=4.01426 EndAngle=5.41052
    g1: ArcOfCircle CenterX=-7.3e-15 CenterY=-7.5 CenterZ=0 NormalX=0 NormalY=0 NormalZ=1 AngleXU=0 Radius=45 StartAngle=4.01426 EndAngle=5.41052
    g2: LineSegment StartX=-28.9254 StartY=-41.972 StartZ=0 EndX=-25.0687 EndY=-37.3757 EndZ=0
    g3: LineSegment StartX=28.9254 StartY=-41.972 StartZ=0 EndX=25.0687 EndY=-37.3757 EndZ=0
  constraints (12):
    c: Coincident(g2,g1)
    c: Coincident(g2,g0)
    c: Coincident(g3,g1)
    c: Coincident(g3,g0)
    c: Coincident(g1,g-4)
    c: Coincident(g0,g1)
    c: Angle(g2,g3) = 1.39626
    c: Angle(g2,g-2) = 0.698132
    c: PointOnObject(g-5,g1)
    c: Tangent(g0,g-3)
    c: PointOnObject(g0,g2)
    c: PointOnObject(g0,g3)
FEATURE [PartDesign::Pocket] Pocket022
  BaseFeature = -> Pocket021
  Direction = (0,-0.987688,-0.156434)
  Length = 0
  Length2 = 5
  Placement = pos=(0,0,0) rot=(1,0,0;1.5708rad)
  Profile = -> Sketch037
  ReferenceAxis = -> Sketch037 [N_Axis]
  Refine = true
  Suppressed = false
  Type = 3
  UpToFace = -> Pocket021 [Face12]
FEATURE [PartDesign::Body] Body  label="Stack_Module_Cover_forinsert001"
  AllowCompound = false
  Group = -> [Sketch,Pad,Fillet,Sketch001,Pad001,Sketch002,Sketch003,Pocket,Sketch004,Pocket001,Sketch005,Pocket002,Sketch006,Pad002,LinearPattern,Sketch007,Pocket003,Sketch008,Pocket004,Sketch009,Pocket005,Sketch010,Pocket006,Fillet001,Fillet002,Fillet003,Fillet004,Fillet005,Pocket007,Mirrored,Sketch014,Sketch015,Pocket012,Sketch016,Pad003,Sketch017,Pocket013,LinearPattern001,Sketch019,Pocket014,Sketch020,+30 more]
  Origin = -> Origin001
  Tip = -> Pocket022
FEATURE [PartDesign::CoordinateSystem] tee_att
  AttacherType = Attacher::AttachEngine3D
  AttachmentSupport = -> [Pocket022]
  MapMode = 11
  Placement = pos=(0,-14.4165,-48.3505) rot=(-0.544663,0.544663,0.637718;2.00621rad)
FEATURE [PartDesign::CoordinateSystem] Logo_att
  AttacherType = Attacher::AttachEngine3D
  AttachmentSupport = -> [Pocket022]
  MapMode = 11
  Placement = pos=(0,-22.7075,3.99697) rot=(-0.544663,0.544663,0.637718;2.00621rad)
FEATURE [PartDesign::CoordinateSystem] sleevenut_att1
  AttacherType = Attacher::AttachEngine3D
  AttachmentSupport = -> [Pocket022]
  MapMode = 11
  Placement = pos=(66.5,-8,-53.5) rot=(0.57735,-0.57735,0.57735;2.0944rad)
FEATURE [PartDesign::CoordinateSystem] sleevenut_att2
  AttacherType = Attacher::AttachEngine3D
  AttachmentSupport = -> [Pocket022]
  MapMode = 11
  Placement = pos=(63.5,-8,62.5) rot=(0.57735,-0.57735,0.57735;2.0944rad)
FEATURE [PartDesign::CoordinateSystem] sleevenut_att3
  AttacherType = Attacher::AttachEngine3D
  AttachmentSupport = -> [Pocket022]
  MapMode = 11
  Placement = pos=(-63.5,-8,62.5) rot=(0.57735,0.57735,0.57735;4.18879rad)
FEATURE [PartDesign::CoordinateSystem] sleevenut_att4
  AttacherType = Attacher::AttachEngine3D
  AttachmentSupport = -> [Pocket022]
  MapMode = 11
  Placement = pos=(-66.5,-8,-53.5) rot=(0.57735,0.57735,0.57735;4.18879rad)
FEATURE [PartDesign::CoordinateSystem] stack_att
  AttacherType = Attacher::AttachEngine3D
  AttachmentSupport = -> [Pocket022]
  MapMode = 11
  Placement = pos=(-63.5,1.41e-14,62.5) rot=(0.57735,0.57735,-0.57735;2.0944rad)
FEATURE [App::Part] Part  label="Stack_Module_Cover_twoInserts"
  Group = -> [Body,tee_att,Logo_att,sleevenut_att1,sleevenut_att2,sleevenut_att3,sleevenut_att4,stack_att]
  Origin = -> Origin
---- part ../../Part/Print/Stack_Module_Cover_insert.FCStd = doc fcstd_c0eddcec3766 ----
FCSTD DOCUMENT  (FreeCAD 1.0R39319 (Git))
Label: Stack_Module_Cover_insert
License: All rights reserved
LicenseURL: https://en.wikipedia.org/wiki/All_rights_reserved
objects: Sketcher::SketchObject×5, PartDesign::Pad×2, PartDesign::Pocket×2, PartDesign::Chamfer×2, PartDesign::Revolution×1, PartDesign::Fillet×1, PartDesign::Mirrored×1, PartDesign::Body×1, PartDesign::CoordinateSystem×1, App::Part×1
note: 38 computed .brp shape members not serialized (recipe doc carries the construction recipe); baked Part::Feature solids carry a one-line shape summary decoded from their .brp

FEATURE [Sketcher::SketchObject] Sketch
  ArcFitTolerance = 1e-06
  AttachmentSupport = -> [XY_Plane001]
  FullyConstrained = true
  MakeInternals = false
  MapMode = 5
  sketch-geometry (1):
    g0: Circle CenterX=0 CenterY=0 CenterZ=0 NormalX=0 NormalY=0 NormalZ=1 AngleXU=0 Radius=38.5
  constraints (2):
    c: Coincident(g0,g-1)
    c: Diameter(g0) = 77
FEATURE [PartDesign::Pad] Pad
  Direction = (0,0,1)
  Length = 2
  Length2 = 10
  Profile = -> Sketch
  ReferenceAxis = -> Sketch [N_Axis]
  Refine = true
  Suppressed = false
  Type = 0
FEATURE [Sketcher::SketchObject] Sketch002
  ArcFitTolerance = 1e-06
  AttachmentSupport = -> [YZ_Plane001]
  ExternalGeometry = -> [Pad]
  FullyConstrained = true
  MakeInternals = false
  MapMode = 5
  Placement = pos=(0,0,0) rot=(0.57735,0.57735,0.57735;2.0944rad)
  sketch-geometry (5):
    g0: LineSegment StartX=38.5 StartY=2 StartZ=0 EndX=0 EndY=2 EndZ=0
    g1: LineSegment StartX=0 StartY=2 StartZ=0 EndX=0 EndY=13 EndZ=0
    g2: LineSegment StartX=38.5 StartY=2 StartZ=0 EndX=38.5 EndY=3 EndZ=0
    g3: ArcOfCircle CenterX=41.1667 CenterY=8 CenterZ=0 NormalX=0 NormalY=0 NormalZ=1 AngleXU=0 Radius=5.66667 StartAngle=2.06075 EndAngle=4.22243
    g4: LineSegment StartX=0 StartY=13 StartZ=0 EndX=38.5 EndY=13 EndZ=0
  constraints (15):
    c: PointOnObject(g0,g-3)
    c: Symmetric(g-3,g-3,g0)
    c: Coincident(g0,g1)
    c: PointOnObject(g1,g-2)
    c: Coincident(g2,g0)
    c: Vertical(g2)
    c: Coincident(g3,g2)
    c: Distance(g2,g1) = 38.5
    c: DistanceY(g2,g2) = 1
    c: DistanceY(g2,g3) = 10
    c: Distance(g3,g2) = -3
    c: PointOnObject(g3,g2)
    c: Coincident(g4,g1)
    c: Coincident(g4,g3)
    c: Horizontal(g4)
FEATURE [PartDesign::Revolution] Revolution
  Angle = 360
  Angle2 = 60
  Axis = (0,0,1)
  Base = (0,0,0)
  BaseFeature = -> Pad
  Profile = -> Sketch002
  ReferenceAxis = -> Sketch002 [V_Axis]
  Refine = true
  Reversed = true
  Suppressed = false
  Type = 0
FEATURE [PartDesign::Fillet] Fillet
  Base = -> Revolution [Edge5]
  BaseFeature = -> Revolution
  Radius = 0.5
  Refine = true
  SupportTransform = false
  Suppressed = false
  UseAllEdges = false
FEATURE [Sketcher::SketchObject] Sketch003
  ArcFitTolerance = 1e-06
  AttachmentSupport = -> [XY_Plane001]
  ExternalGeometry = -> [Fillet]
  FullyConstrained = true
  MakeInternals = false
  MapMode = 5
  sketch-geometry (10):
    g0: LineSegment StartX=15.6817 StartY=-35.1615 StartZ=0 EndX=16.7859 EndY=-37.074 EndZ=0
    g1: ArcOfCircle CenterX=20.25 CenterY=-35.074 CenterZ=0 NormalX=0 NormalY=0 NormalZ=1 AngleXU=0 Radius=4 StartAngle=3.66519 EndAngle=6.80678
    g2: LineSegment StartX=23.7141 StartY=-33.074 StartZ=0 EndX=22.6099 EndY=-31.1615 EndZ=0
    g3: ArcOfCircle CenterX=0 CenterY=0 CenterZ=0 NormalX=0 NormalY=0 NormalZ=1 AngleXU=0 Radius=38.5 StartAngle=5.1319 EndAngle=5.34007
    g4: LineSegment [constr] StartX=20.25 StartY=-35.074 StartZ=0 EndX=19.25 EndY=-33.342 EndZ=0
    g5: LineSegment StartX=-15.6817 StartY=-35.1615 StartZ=0 EndX=-16.7859 EndY=-37.074 EndZ=0
    g6: ArcOfCircle CenterX=-20.25 CenterY=-35.074 CenterZ=0 NormalX=0 NormalY=0 NormalZ=1 AngleXU=0 Radius=4 StartAngle=2.61799 EndAngle=5.75959
    g7: LineSegment StartX=-23.7141 StartY=-33.074 StartZ=0 EndX=-22.6099 EndY=-31.1615 EndZ=0
    g8: ArcOfCircle CenterX=0 CenterY=0 CenterZ=0 NormalX=0 NormalY=0 NormalZ=1 AngleXU=0 Radius=38.5 StartAngle=4.08471 EndAngle=4.29287
    g9: LineSegment [constr] StartX=-20.25 StartY=-35.074 StartZ=0 EndX=-19.25 EndY=-33.342 EndZ=0
  constraints (28):
    c: Tangent(g0,g1) = -1.5708
    c: Tangent(g1,g2) = -1.5708
    c: Coincident(g3,g0)
    c: Coincident(g3,g2)
    c: Coincident(g3,g-1)
    c: Coincident(g4,g1)
    c: PointOnObject(g4,g3)
    c: PointOnObject(g3,g4)
    c: Parallel(g0,g2)
    c: Distance(g2,g0) = 8
    c: Distance(g4,g4) = 2
    c: Parallel(g0,g4)
    c: PointOnObject(g4,g-3)
    c: Angle(g-2,g4) = 0.523599
    c: Tangent(g5,g6) = 1.5708
    c: Tangent(g6,g7) = 1.5708
    c: Coincident(g8,g5)
    c: Coincident(g8,g7)
    c: Coincident(g9,g6)
    c: PointOnObject(g9,g8)
    c: PointOnObject(g8,g9)
    c: Parallel(g5,g7)
    c: Distance(g7,g5) = 8
    c: Distance(g9,g9) = 2
    c: Parallel(g5,g9)
    c: PointOnObject(g9,g-3)
    c: Angle(g9,g-2) = 0.523599
    c: Coincident(g3,g8)
FEATURE [PartDesign::Pad] Pad001
  BaseFeature = -> Fillet
  Direction = (0,0,1)
  Length = 3
  Length2 = -2
  Profile = -> Sketch003
  ReferenceAxis = -> Sketch003 [N_Axis]
  Refine = true
  Suppressed = false
  Type = 4
FEATURE [PartDesign::Mirrored] Mirrored
  BaseFeature = -> Pad001
  MirrorPlane = -> XZ_Plane001
  Originals = -> [Pad001]
  Refine = true
  Suppressed = false
  TransformMode = 0
FEATURE [Sketcher::SketchObject] Sketch004
  ArcFitTolerance = 1e-06
  AttachmentSupport = -> [Mirrored]
  FullyConstrained = true
  MakeInternals = false
  MapMode = 5
  Placement = pos=(0,0,0) rot=(1,0,0;3.14159rad)
  sketch-geometry (8):
    g0: LineSegment [constr] StartX=0 StartY=0 StartZ=0 EndX=-30.0366 EndY=5.29627 EndZ=0
    g1: Circle CenterX=-30.0366 CenterY=5.29627 CenterZ=0 NormalX=0 NormalY=0 NormalZ=1 AngleXU=0 Radius=3
    g2: Circle CenterX=-20.8451 CenterY=-9.72022 CenterZ=0 NormalX=0 NormalY=0 NormalZ=1 AngleXU=0 Radius=3
    g3: Circle CenterX=-15.686 CenterY=16.8211 CenterZ=0 NormalX=0 NormalY=0 NormalZ=1 AngleXU=0 Radius=3
    g4: Circle CenterX=22.6506 CenterY=-3.99391 CenterZ=0 NormalX=0 NormalY=0 NormalZ=1 AngleXU=0 Radius=3
    g5: LineSegment [constr] StartX=-15.686 StartY=16.8211 StartZ=0 EndX=0 EndY=0 EndZ=0
    g6: LineSegment [constr] StartX=-20.8451 StartY=-9.72022 StartZ=0 EndX=0 EndY=0 EndZ=0
    g7: LineSegment [constr] StartX=0 StartY=0 StartZ=0 EndX=22.6506 EndY=-3.99391 EndZ=0
  constraints (20):
    c: Coincident(g0,g-1)
    c: Angle(g-1,g0) = -0.174533
    c: Coincident(g5,g3)
    c: Coincident(g5,g0)
    c: Coincident(g6,g2)
    c: Coincident(g6,g0)
    c: Coincident(g7,g0)
    c: Coincident(g7,g4)
    c: Angle(g5,g0) = 0.645772
    c: Angle(g0,g6) = 0.610865
    c: Angle(g7,g0) = 3.14159
    c: Distance(g5,g5) = 23
    c: Distance(g6,g6) = 23
    c: Coincident(g0,g1)
    c: Distance(g0,g0) = 30.5
    c: Diameter(g3) = 6
    c: Diameter(g1) = 6
    c: Diameter(g2) = 6
    c: Diameter(g4) = 6
    c: Distance(g7,g7) = 23
FEATURE [PartDesign::Pocket] Pocket
  BaseFeature = -> Mirrored
  Direction = (0,0,1)
  Length = 0
  Length2 = 5
  Offset = -1
  Profile = -> Sketch004
  ReferenceAxis = -> Sketch004 [N_Axis]
  Refine = true
  Suppressed = false
  Type = 3
  UpToFace = -> Mirrored [Face1]
FEATURE [PartDesign::Chamfer] Chamfer
  Angle = 45
  Base = -> Pocket [Edge64,Edge61,Edge63,Edge62]
  BaseFeature = -> Pocket
  ChamferType = 0
  FlipDirection = false
  Refine = true
  Size = 0.5
  Size2 = 1
  SupportTransform = false
  Suppressed = false
  UseAllEdges = false
FEATURE [PartDesign::Chamfer] Chamfer001
  Angle = 45
  Base = -> Chamfer [Edge70,Edge74,Edge72,Edge34]
  BaseFeature = -> Chamfer
  ChamferType = 0
  FlipDirection = false
  Refine = true
  Size = 1.5
  Size2 = 1
  SupportTransform = false
  Suppressed = false
  UseAllEdges = false
FEATURE [Sketcher::SketchObject] Sketch005
  ArcFitTolerance = 1e-06
  AttachmentSupport = -> [Chamfer001]
  ExternalGeometry = -> [Chamfer001]
  FullyConstrained = true
  MakeInternals = false
  MapMode = 5
  Placement = pos=(0,0,12) rot=(1,0,0;3.14159rad)
  sketch-geometry (4):
    g0: Circle CenterX=-15.686 CenterY=16.8211 CenterZ=0 NormalX=0 NormalY=0 NormalZ=1 AngleXU=0 Radius=1.50001
    g1: Circle CenterX=-30.0366 CenterY=5.29627 CenterZ=0 NormalX=0 NormalY=0 NormalZ=1 AngleXU=0 Radius=1.50001
    g2: Circle CenterX=-20.8451 CenterY=-9.72022 CenterZ=0 NormalX=0 NormalY=0 NormalZ=1 AngleXU=0 Radius=1.50001
    g3: Circle CenterX=22.6506 CenterY=-3.99391 CenterZ=0 NormalX=0 NormalY=0 NormalZ=1 AngleXU=0 Radius=1.50001
  constraints (8):
    c: Coincident(g0,g-4)
    c: Coincident(g1,g-5)
    c: Coincident(g2,g-6)
    c: Coincident(g3,g-3)
    c: Tangent(g-4,g0)
    c: Tangent(g-5,g1)
    c: Tangent(g-6,g2)
    c: Tangent(g-3,g3)
FEATURE [PartDesign::Pocket] Pocket001
  BaseFeature = -> Chamfer001
  Direction = (0,0,1)
  Length = 5
  Length2 = 5
  Profile = -> Sketch005
  ReferenceAxis = -> Sketch005 [N_Axis]
  Refine = true
  Suppressed = false
  Type = 1
FEATURE [PartDesign::Body] Body  label="Stack_Module_Cover_insert001"
  AllowCompound = false
  Group = -> [Sketch,Pad,Sketch002,Revolution,Fillet,Sketch003,Pad001,Mirrored,Sketch004,Pocket,Chamfer,Chamfer001,Sketch005,Pocket001]
  Origin = -> Origin001
  Tip = -> Pocket001
FEATURE [PartDesign::CoordinateSystem] LCS_1
  AttacherType = Attacher::AttachEngine3D
  AttachmentOffset = pos=(0,0,0) rot=(0,0,1;0.174533rad)
  AttachmentSupport = -> [Pocket001]
  MapMode = 11
  Placement = pos=(0,0,0) rot=(0,0,1;3.31613rad)
FEATURE [App::Part] Part  label="Stack_Module_Cover_insert"
  Group = -> [Body,LCS_1]
  Origin = -> Origin
---- part ../../Part/Purchase/M5x12_Sleeve_Nut.FCStd = doc fcstd_530124feeac1 ----
FCSTD DOCUMENT  (FreeCAD 1.0R39319 (Git))
Label: M5x12_Sleeve_Nut
License: All rights reserved
LicenseURL: https://en.wikipedia.org/wiki/All_rights_reserved
objects: Sketcher::SketchObject×3, PartDesign::Pocket×2, PartDesign::Revolution×1, PartDesign::Fillet×1, PartDesign::Body×1, PartDesign::CoordinateSystem×1, App::Part×1
note: 20 computed .brp shape members not serialized (recipe doc carries the construction recipe); baked Part::Feature solids carry a one-line shape summary decoded from their .brp

FEATURE [Sketcher::SketchObject] Sketch
  ArcFitTolerance = 1e-06
  AttachmentSupport = -> [XZ_Plane001]
  FullyConstrained = true
  MakeInternals = false
  MapMode = 5
  Placement = pos=(0,0,0) rot=(1,0,0;1.5708rad)
  sketch-geometry (7):
    g0: LineSegment StartX=0 StartY=-12 StartZ=0 EndX=0 EndY=2 EndZ=0
    g1: LineSegment StartX=0 StartY=2 StartZ=0 EndX=3.75 EndY=2 EndZ=0
    g2: LineSegment StartX=3.75 StartY=2 StartZ=0 EndX=5.35 EndY=1.5 EndZ=0
    g3: LineSegment StartX=5.35 StartY=1.5 StartZ=0 EndX=5.35 EndY=0 EndZ=0
    g4: LineSegment StartX=5.35 StartY=0 StartZ=0 EndX=2.9 EndY=0 EndZ=0
    g5: LineSegment StartX=2.9 StartY=0 StartZ=0 EndX=2.9 EndY=-12 EndZ=0
    g6: LineSegment StartX=2.9 StartY=-12 StartZ=0 EndX=0 EndY=-12 EndZ=0
  constraints (21):
    c: PointOnObject(g0,g-2)
    c: PointOnObject(g0,g-2)
    c: Coincident(g0,g1)
    c: Horizontal(g1)
    c: Coincident(g1,g2)
    c: Coincident(g2,g3)
    c: Vertical(g3)
    c: Coincident(g3,g4)
    c: Horizontal(g4)
    c: Coincident(g4,g5)
    c: Vertical(g5)
    c: Coincident(g5,g6)
    c: Coincident(g6,g0)
    c: Horizontal(g6)
    c: Distance(g5,g0) = 2.9
    c: DistanceY(g5,g5) = 12
    c: Distance(g4,g1) = 2
    c: Distance(g3,g3) = 1.5
    c: DistanceX(g1,g1) = 3.75
    c: PointOnObject(g4,g-1)
    c: Distance(g-2,g3) = 5.35
FEATURE [PartDesign::Revolution] Revolution
  Angle = 360
  Angle2 = 60
  Axis = (0,2e-16,1)
  Base = (0,0,0)
  Placement = pos=(0,0,0) rot=(1,0,0;1.5708rad)
  Profile = -> Sketch
  ReferenceAxis = -> Sketch [V_Axis]
  Refine = true
  Reversed = true
  Suppressed = false
  Type = 0
FEATURE [Sketcher::SketchObject] Sketch001
  ArcFitTolerance = 1e-06
  AttachmentSupport = -> [Revolution]
  FullyConstrained = true
  MakeInternals = false
  MapMode = 5
  Placement = pos=(0,-5.3e-15,-12) rot=(1,0,0;3.14159rad)
  sketch-geometry (1):
    g0: Circle CenterX=0 CenterY=0 CenterZ=0 NormalX=0 NormalY=0 NormalZ=1 AngleXU=0 Radius=2.15
  constraints (2):
    c: Coincident(g0,g-1)
    c: Diameter(g0) = 4.3
FEATURE [PartDesign::Pocket] Pocket
  BaseFeature = -> Revolution
  Direction = (0,0,1)
  Length = 9.2
  Length2 = 5
  Placement = pos=(0,0,0) rot=(1,0,0;1.5708rad)
  Profile = -> Sketch001
  ReferenceAxis = -> Sketch001 [N_Axis]
  Refine = true
  Suppressed = false
  Type = 0
FEATURE [Sketcher::SketchObject] Sketch002
  ArcFitTolerance = 1e-06
  AttachmentSupport = -> [Pocket]
  FullyConstrained = true
  MakeInternals = false
  MapMode = 5
  Placement = pos=(0,9e-16,2) rot=(0,0,1;3.14159rad)
  sketch-geometry (7):
    g0: LineSegment StartX=1.55 StartY=0.894893 StartZ=0 EndX=0 EndY=1.78979 EndZ=0
    g1: LineSegment StartX=0 StartY=1.78979 StartZ=0 EndX=-1.55 EndY=0.894893 EndZ=0
    g2: LineSegment StartX=-1.55 StartY=0.894893 StartZ=0 EndX=-1.55 EndY=-0.894893 EndZ=0
    g3: LineSegment StartX=-1.55 StartY=-0.894893 StartZ=0 EndX=4e-16 EndY=-1.78979 EndZ=0
    g4: LineSegment StartX=4e-16 StartY=-1.78979 StartZ=0 EndX=1.55 EndY=-0.894893 EndZ=0
    g5: LineSegment StartX=1.55 StartY=-0.894893 StartZ=0 EndX=1.55 EndY=0.894893 EndZ=0
    g6: Circle [constr] CenterX=0 CenterY=0 CenterZ=0 NormalX=0 NormalY=0 NormalZ=1 AngleXU=0 Radius=1.78979
  constraints (16):
    c: Coincident(g0,g1)
    c: Coincident(g1,g2)
    c: Coincident(g2,g3)
    c: Coincident(g3,g4)
    c: Coincident(g4,g5)
    c: Coincident(g5,g0)
    c: Equal(g0, g1-g5) x5
    c: PointOnObject(g0,g6)
    c: PointOnObject(g1,g6)
    c: PointOnObject(g2,g6)
    c: PointOnObject(g3,g6)
    c: PointOnObject(g4,g6)
    c: PointOnObject(g5,g6)
    c: Coincident(g6,g-1)
    c: Distance(g5,g2) = 3.1
    c: PointOnObject(g0,g-2)
FEATURE [PartDesign::Pocket] Pocket001
  BaseFeature = -> Pocket
  Direction = (0,0,-1)
  Length = 2.2
  Length2 = 5
  Placement = pos=(0,0,0) rot=(1,0,0;1.5708rad)
  Profile = -> Sketch002
  ReferenceAxis = -> Sketch002 [N_Axis]
  Refine = true
  Suppressed = false
  Type = 0
FEATURE [PartDesign::Fillet] Fillet
  Base = -> Pocket001 [Edge22,Edge8,Edge1,Edge25,Edge24]
  BaseFeature = -> Pocket001
  Placement = pos=(0,0,0) rot=(1,0,0;1.5708rad)
  Radius = 0.2
  Refine = true
  SupportTransform = false
  Suppressed = false
  UseAllEdges = false
FEATURE [PartDesign::Body] Body  label="M5x12_Sleeve_Nut001"
  AllowCompound = false
  Group = -> [Sketch,Revolution,Sketch001,Pocket,Sketch002,Pocket001,Fillet]
  Origin = -> Origin001
  Tip = -> Fillet
FEATURE [PartDesign::CoordinateSystem] LCS_1
  AttacherType = Attacher::AttachEngine3D
  AttachmentSupport = -> [Fillet]
  MapMode = 11
  Placement = pos=(4e-16,0,0) rot=(0.707107,-0.707107,0;3.14159rad)
FEATURE [App::Part] Part  label="M5x12_Sleeve_Nut"
  Group = -> [Body,LCS_1]
  Origin = -> Origin
